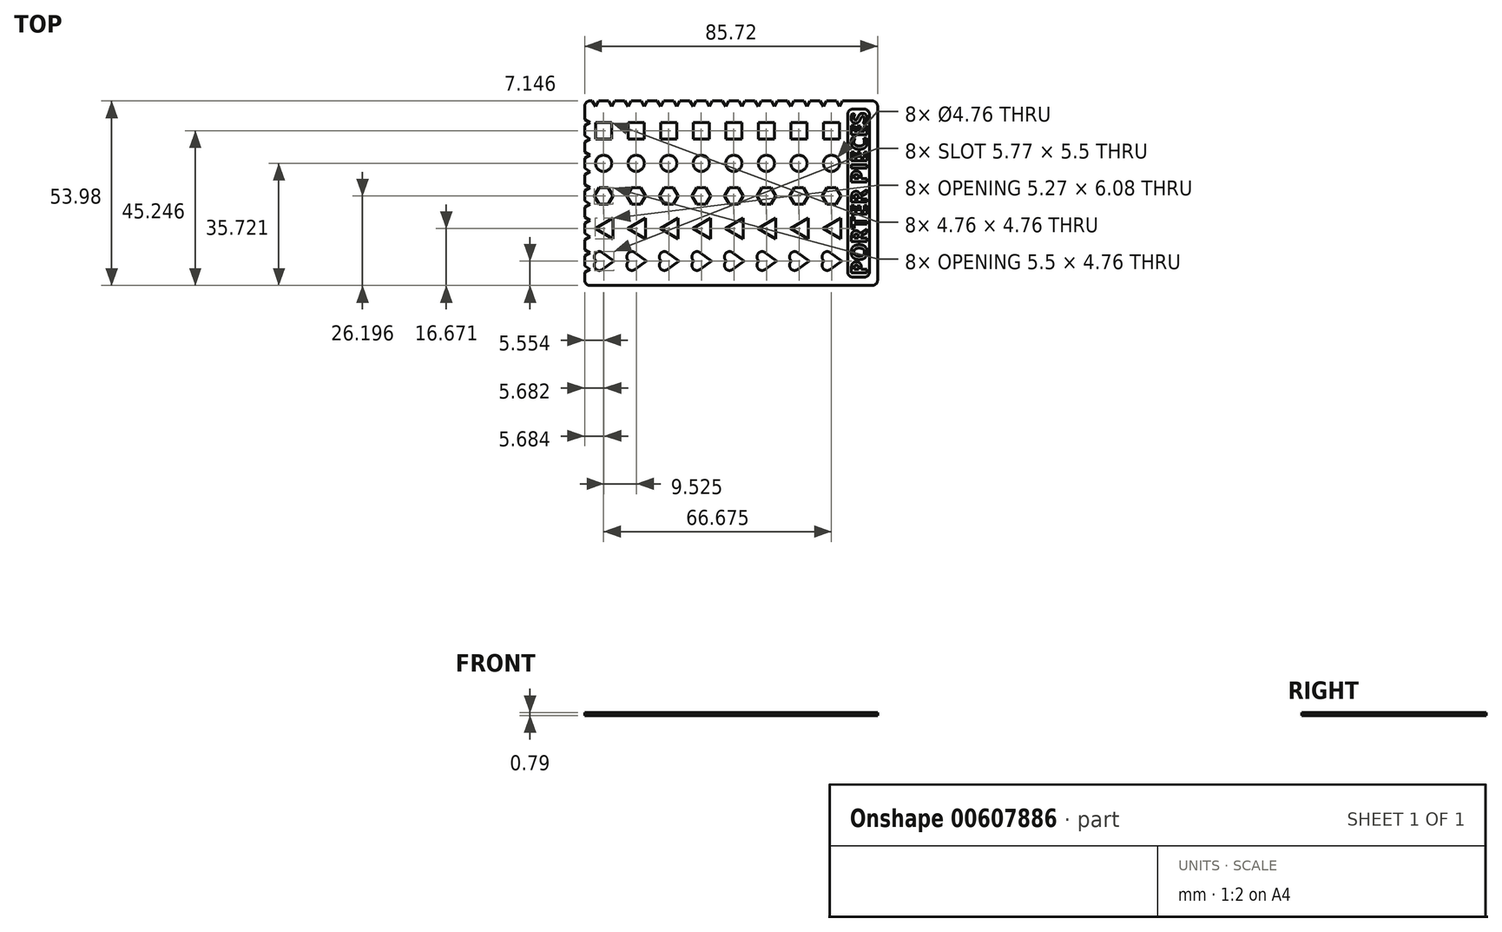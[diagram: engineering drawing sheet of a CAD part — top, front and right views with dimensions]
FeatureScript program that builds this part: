
annotation { "Feature Type Name" : "Feature", "Feature Type Description" : "" }
export const myFeature = defineFeature(function(context is Context, id is Id, definition is map)
    precondition{}
    {
        {
            var Q0;
            Q0=qCreatedBy(makeId("Top.planeOp"),FACE);
            var sketch = newSketch(context, id + "F0", { "sketchPlane" : qUnion([Q0])});
            skLineSegment(sketch, "E0.bottom", {"start": v(42.86, 26.99) * mm, "end": v(-42.86, 26.99) * mm});
            skLineSegment(sketch, "E0.top", {"start": v(42.86, -26.99) * mm, "end": v(-42.86, -26.99) * mm});
            skLineSegment(sketch, "E0.left", {"start": v(42.86, 26.99) * mm, "end": v(42.86, -26.99) * mm});
            skLineSegment(sketch, "E0.right", {"start": v(-42.86, 26.99) * mm, "end": v(-42.86, -26.99) * mm});
            skPoint(sketch, "E0.middle", {"position": v(0, 0) * mm});
            skSolve(sketch);
        }
        {
            var Q0;
            Q0=makeQuery(id+"F0.imprint","IMPRINT",FACE,{"disambiguationData":[TD([[makeQuery(id+"F0.imprint","IMPRINT",EDGE,{"derivedFrom":sQuery(id+"F0.wireOp",EDGE,"E0.bottom")}),1.0]])]});
            extrude(context, id + "F1", {"entities" : qUnion([Q0]), "depth" : 0.8 * mm, "offsetDistance" : 25.4 * mm});
        }
        {
            var Q0;
            Q0=makeQuery(id+"F1.opExtrude","SWEPT_EDGE",EDGE,{"disambiguationData":[OSD([sQuery(id+"F0.wireOp",EDGE,"E0.bottom"),sQuery(id+"F0.wireOp",EDGE,"E0.left")])]});
            var Q1;
            Q1=makeQuery(id+"F1.opExtrude","SWEPT_EDGE",EDGE,{"disambiguationData":[OSD([sQuery(id+"F0.wireOp",EDGE,"E0.bottom"),sQuery(id+"F0.wireOp",EDGE,"E0.right")])]});
            var Q2;
            Q2=makeQuery(id+"F1.opExtrude","SWEPT_EDGE",EDGE,{"disambiguationData":[OSD([sQuery(id+"F0.wireOp",EDGE,"E0.top"),sQuery(id+"F0.wireOp",EDGE,"E0.right")])]});
            var Q3;
            Q3=makeQuery(id+"F1.opExtrude","SWEPT_EDGE",EDGE,{"disambiguationData":[OSD([sQuery(id+"F0.wireOp",EDGE,"E0.top"),sQuery(id+"F0.wireOp",EDGE,"E0.left")])]});
            fillet(context, id + "F2", {"entities" : qUnion([Q0, Q1, Q2, Q3]), "radius" : 1.59 * mm, "tangentPropagation" : true, "allowEdgeOverflow" : false});
        }
        {
            var Q0;
            Q0=makeQuery(id+"F1.opExtrude","CAP_FACE",FACE,{"disambiguationData":[OSD([sQuery(id+"F0.wireOp",EDGE,"E0.bottom"),sQuery(id+"F0.wireOp",EDGE,"E0.top"),sQuery(id+"F0.wireOp",EDGE,"E0.left"),sQuery(id+"F0.wireOp",EDGE,"E0.right")])],"isStart":false});
            var sketch = newSketch(context, id + "F3", { "sketchPlane" : qUnion([Q0])});
            skLineSegment(sketch, "E1.bottom", {"start": v(-39.69, 20.64) * mm, "end": v(-34.92, 20.64) * mm});
            skLineSegment(sketch, "E1.top", {"start": v(-39.69, 15.88) * mm, "end": v(-34.92, 15.88) * mm});
            skLineSegment(sketch, "E1.left", {"start": v(-39.69, 20.64) * mm, "end": v(-39.69, 15.88) * mm});
            skLineSegment(sketch, "E1.right", {"start": v(-34.92, 20.64) * mm, "end": v(-34.92, 15.88) * mm});
            skLineSegment(sketch, "E2.1.0.0", {"start": v(-25.4, 20.64) * mm, "end": v(-25.4, 15.88) * mm});
            skLineSegment(sketch, "E2.1.0.1", {"start": v(-30.16, 20.64) * mm, "end": v(-30.16, 15.88) * mm});
            skLineSegment(sketch, "E2.1.0.2", {"start": v(-30.16, 15.88) * mm, "end": v(-25.4, 15.88) * mm});
            skLineSegment(sketch, "E2.1.0.3", {"start": v(-30.16, 20.64) * mm, "end": v(-25.4, 20.64) * mm});
            skLineSegment(sketch, "E2.2.0.0", {"start": v(-15.88, 20.64) * mm, "end": v(-15.88, 15.88) * mm});
            skLineSegment(sketch, "E2.2.0.1", {"start": v(-20.64, 20.64) * mm, "end": v(-20.64, 15.88) * mm});
            skLineSegment(sketch, "E2.2.0.2", {"start": v(-20.64, 15.88) * mm, "end": v(-15.88, 15.88) * mm});
            skLineSegment(sketch, "E2.2.0.3", {"start": v(-20.64, 20.64) * mm, "end": v(-15.88, 20.64) * mm});
            skLineSegment(sketch, "E2.3.0.0", {"start": v(-6.35, 20.64) * mm, "end": v(-6.35, 15.88) * mm});
            skLineSegment(sketch, "E2.3.0.1", {"start": v(-11.11, 20.64) * mm, "end": v(-11.11, 15.88) * mm});
            skLineSegment(sketch, "E2.3.0.2", {"start": v(-11.11, 15.88) * mm, "end": v(-6.35, 15.88) * mm});
            skLineSegment(sketch, "E2.3.0.3", {"start": v(-11.11, 20.64) * mm, "end": v(-6.35, 20.64) * mm});
            skLineSegment(sketch, "E2.4.0.0", {"start": v(3.17, 20.64) * mm, "end": v(3.17, 15.88) * mm});
            skLineSegment(sketch, "E2.4.0.1", {"start": v(-1.59, 20.64) * mm, "end": v(-1.59, 15.88) * mm});
            skLineSegment(sketch, "E2.4.0.2", {"start": v(-1.59, 15.88) * mm, "end": v(3.17, 15.88) * mm});
            skLineSegment(sketch, "E2.4.0.3", {"start": v(-1.59, 20.64) * mm, "end": v(3.17, 20.64) * mm});
            skLineSegment(sketch, "E2.5.0.0", {"start": v(12.7, 20.64) * mm, "end": v(12.7, 15.88) * mm});
            skLineSegment(sketch, "E2.5.0.1", {"start": v(7.94, 20.64) * mm, "end": v(7.94, 15.88) * mm});
            skLineSegment(sketch, "E2.5.0.2", {"start": v(7.94, 15.88) * mm, "end": v(12.7, 15.88) * mm});
            skLineSegment(sketch, "E2.5.0.3", {"start": v(7.94, 20.64) * mm, "end": v(12.7, 20.64) * mm});
            skLineSegment(sketch, "E2.6.0.0", {"start": v(22.22, 20.64) * mm, "end": v(22.22, 15.88) * mm});
            skLineSegment(sketch, "E2.6.0.1", {"start": v(17.46, 20.64) * mm, "end": v(17.46, 15.88) * mm});
            skLineSegment(sketch, "E2.6.0.2", {"start": v(17.46, 15.88) * mm, "end": v(22.22, 15.88) * mm});
            skLineSegment(sketch, "E2.6.0.3", {"start": v(17.46, 20.64) * mm, "end": v(22.22, 20.64) * mm});
            skLineSegment(sketch, "E2.7.0.0", {"start": v(31.75, 20.64) * mm, "end": v(31.75, 15.88) * mm});
            skLineSegment(sketch, "E2.7.0.1", {"start": v(26.99, 20.64) * mm, "end": v(26.99, 15.88) * mm});
            skLineSegment(sketch, "E2.7.0.2", {"start": v(26.99, 15.88) * mm, "end": v(31.75, 15.88) * mm});
            skLineSegment(sketch, "E2.7.0.3", {"start": v(26.99, 20.64) * mm, "end": v(31.75, 20.64) * mm});
            skLineSegment(sketch, "E2.direction1", {"start": v(-39.69, 15.88) * mm, "end": v(-30.16, 15.88) * mm, "construction": true});
            skSolve(sketch);
        }
        {
            var Q0;
            Q0=makeQuery(id+"F3.imprint","IMPRINT",FACE,{"disambiguationData":[TD([[makeQuery(id+"F3.imprint","IMPRINT",EDGE,{"derivedFrom":sQuery(id+"F3.wireOp",EDGE,"E1.bottom")}),-1.0]])]});
            var Q1;
            Q1=makeQuery(id+"F3.imprint","IMPRINT",FACE,{"disambiguationData":[TD([[makeQuery(id+"F3.imprint","IMPRINT",EDGE,{"derivedFrom":sQuery(id+"F3.wireOp",EDGE,"E2.1.0.0")}),-1.0]])]});
            var Q2;
            Q2=makeQuery(id+"F3.imprint","IMPRINT",FACE,{"disambiguationData":[TD([[makeQuery(id+"F3.imprint","IMPRINT",EDGE,{"derivedFrom":sQuery(id+"F3.wireOp",EDGE,"E2.2.0.0")}),-1.0]])]});
            var Q3;
            Q3=makeQuery(id+"F3.imprint","IMPRINT",FACE,{"disambiguationData":[TD([[makeQuery(id+"F3.imprint","IMPRINT",EDGE,{"derivedFrom":sQuery(id+"F3.wireOp",EDGE,"E2.3.0.0")}),-1.0]])]});
            var Q4;
            Q4=makeQuery(id+"F3.imprint","IMPRINT",FACE,{"disambiguationData":[TD([[makeQuery(id+"F3.imprint","IMPRINT",EDGE,{"derivedFrom":sQuery(id+"F3.wireOp",EDGE,"E2.4.0.0")}),-1.0]])]});
            var Q5;
            Q5=makeQuery(id+"F3.imprint","IMPRINT",FACE,{"disambiguationData":[TD([[makeQuery(id+"F3.imprint","IMPRINT",EDGE,{"derivedFrom":sQuery(id+"F3.wireOp",EDGE,"E2.5.0.0")}),-1.0]])]});
            var Q6;
            Q6=makeQuery(id+"F3.imprint","IMPRINT",FACE,{"disambiguationData":[TD([[makeQuery(id+"F3.imprint","IMPRINT",EDGE,{"derivedFrom":sQuery(id+"F3.wireOp",EDGE,"E2.6.0.0")}),-1.0]])]});
            var Q7;
            Q7=makeQuery(id+"F3.imprint","IMPRINT",FACE,{"disambiguationData":[TD([[makeQuery(id+"F3.imprint","IMPRINT",EDGE,{"derivedFrom":sQuery(id+"F3.wireOp",EDGE,"E2.7.0.0")}),-1.0]])]});
            var Q8;
            Q8=makeQuery(id+"F3.imprint","IMPRINT",FACE,{"disambiguationData":[TD([[makeQuery(id+"F3.imprint","IMPRINT",EDGE,{"derivedFrom":sQuery(id+"F3.wireOp",EDGE,"E2.8.0.0")}),-1.0]])]});
            extrude(context, id + "F4", {"entities" : qUnion([Q0, Q1, Q2, Q3, Q4, Q5, Q6, Q7, Q8]), "operationType" : NewBodyOperationType.REMOVE, "oppositeDirection" : true, "depth" : 25.4 * mm, "offsetDistance" : 25.4 * mm});
        }
        {
            var Q0;
            Q0=makeQuery(id+"F1.opExtrude","CAP_FACE",FACE,{"disambiguationData":[OSD([sQuery(id+"F0.wireOp",EDGE,"E0.bottom"),sQuery(id+"F0.wireOp",EDGE,"E0.top"),sQuery(id+"F0.wireOp",EDGE,"E0.left"),sQuery(id+"F0.wireOp",EDGE,"E0.right")])],"isStart":false});
            var sketch = newSketch(context, id + "F5", { "sketchPlane" : qUnion([Q0])});
            skLineSegment(sketch, "E3", {"start": v(-34.92, 25.44) * mm, "end": v(-34.92, 26.99) * mm, "construction": true});
            skLineSegment(sketch, "E4.0", {"start": v(41.27, 26.99) * mm, "end": v(-41.28, 26.99) * mm, "construction": true});
            skLineSegment(sketch, "E5", {"start": v(-34.92, 26.99) * mm, "end": v(-34.92, 34.22) * mm, "construction": true});
            skCircle(sketch, "E6.cCircle", {"center": v(-34.92, 26.99) * mm, "radius": 0.8 * mm, "construction": true});
            skLineSegment(sketch, "E6.0", {"start": v(-36.3, 27.78) * mm, "end": v(-33.55, 27.78) * mm});
            skLineSegment(sketch, "E6.1", {"start": v(-33.55, 27.78) * mm, "end": v(-34.93, 25.4) * mm});
            skLineSegment(sketch, "E6.2", {"start": v(-34.92, 25.4) * mm, "end": v(-36.3, 27.78) * mm});
            skPoint(sketch, "E6.0.midPoint", {"position": v(-34.92, 27.78) * mm});
            skPoint(sketch, "E7.1.0.0", {"position": v(-30.16, 27.78) * mm});
            skLineSegment(sketch, "E7.1.0.1", {"start": v(-30.16, 25.4) * mm, "end": v(-31.54, 27.78) * mm});
            skLineSegment(sketch, "E7.1.0.2", {"start": v(-28.79, 27.78) * mm, "end": v(-30.16, 25.4) * mm});
            skLineSegment(sketch, "E7.1.0.3", {"start": v(-31.54, 27.78) * mm, "end": v(-28.79, 27.78) * mm});
            skCircle(sketch, "E7.1.0.4", {"center": v(-30.16, 26.99) * mm, "radius": 0.8 * mm, "construction": true});
            skPoint(sketch, "E7.2.0.0", {"position": v(-25.4, 27.78) * mm});
            skLineSegment(sketch, "E7.2.0.1", {"start": v(-25.4, 25.4) * mm, "end": v(-26.77, 27.78) * mm});
            skLineSegment(sketch, "E7.2.0.2", {"start": v(-24.03, 27.78) * mm, "end": v(-25.4, 25.4) * mm});
            skLineSegment(sketch, "E7.2.0.3", {"start": v(-26.77, 27.78) * mm, "end": v(-24.03, 27.78) * mm});
            skCircle(sketch, "E7.2.0.4", {"center": v(-25.4, 26.99) * mm, "radius": 0.8 * mm, "construction": true});
            skPoint(sketch, "E7.3.0.0", {"position": v(-20.64, 27.78) * mm});
            skLineSegment(sketch, "E7.3.0.1", {"start": v(-20.64, 25.4) * mm, "end": v(-22.01, 27.78) * mm});
            skLineSegment(sketch, "E7.3.0.2", {"start": v(-19.26, 27.78) * mm, "end": v(-20.64, 25.4) * mm});
            skLineSegment(sketch, "E7.3.0.3", {"start": v(-22.01, 27.78) * mm, "end": v(-19.26, 27.78) * mm});
            skCircle(sketch, "E7.3.0.4", {"center": v(-20.64, 26.99) * mm, "radius": 0.8 * mm, "construction": true});
            skPoint(sketch, "E7.4.0.0", {"position": v(-15.87, 27.78) * mm});
            skLineSegment(sketch, "E7.4.0.1", {"start": v(-15.87, 25.4) * mm, "end": v(-17.25, 27.78) * mm});
            skLineSegment(sketch, "E7.4.0.2", {"start": v(-14.5, 27.78) * mm, "end": v(-15.87, 25.4) * mm});
            skLineSegment(sketch, "E7.4.0.3", {"start": v(-17.25, 27.78) * mm, "end": v(-14.5, 27.78) * mm});
            skCircle(sketch, "E7.4.0.4", {"center": v(-15.87, 26.99) * mm, "radius": 0.8 * mm, "construction": true});
            skPoint(sketch, "E7.5.0.0", {"position": v(-11.11, 27.78) * mm});
            skLineSegment(sketch, "E7.5.0.1", {"start": v(-11.11, 25.4) * mm, "end": v(-12.49, 27.78) * mm});
            skLineSegment(sketch, "E7.5.0.2", {"start": v(-9.74, 27.78) * mm, "end": v(-11.11, 25.4) * mm});
            skLineSegment(sketch, "E7.5.0.3", {"start": v(-12.49, 27.78) * mm, "end": v(-9.74, 27.78) * mm});
            skCircle(sketch, "E7.5.0.4", {"center": v(-11.11, 26.99) * mm, "radius": 0.8 * mm, "construction": true});
            skPoint(sketch, "E7.6.0.0", {"position": v(-6.35, 27.78) * mm});
            skLineSegment(sketch, "E7.6.0.1", {"start": v(-6.35, 25.4) * mm, "end": v(-7.72, 27.78) * mm});
            skLineSegment(sketch, "E7.6.0.2", {"start": v(-4.98, 27.78) * mm, "end": v(-6.35, 25.4) * mm});
            skLineSegment(sketch, "E7.6.0.3", {"start": v(-7.72, 27.78) * mm, "end": v(-4.98, 27.78) * mm});
            skCircle(sketch, "E7.6.0.4", {"center": v(-6.35, 26.99) * mm, "radius": 0.8 * mm, "construction": true});
            skPoint(sketch, "E7.7.0.0", {"position": v(-1.59, 27.78) * mm});
            skLineSegment(sketch, "E7.7.0.1", {"start": v(-1.59, 25.4) * mm, "end": v(-2.96, 27.78) * mm});
            skLineSegment(sketch, "E7.7.0.2", {"start": v(-0.21, 27.78) * mm, "end": v(-1.59, 25.4) * mm});
            skLineSegment(sketch, "E7.7.0.3", {"start": v(-2.96, 27.78) * mm, "end": v(-0.21, 27.78) * mm});
            skCircle(sketch, "E7.7.0.4", {"center": v(-1.59, 26.99) * mm, "radius": 0.8 * mm, "construction": true});
            skPoint(sketch, "E7.8.0.0", {"position": v(3.18, 27.78) * mm});
            skLineSegment(sketch, "E7.8.0.1", {"start": v(3.18, 25.4) * mm, "end": v(1.8, 27.78) * mm});
            skLineSegment(sketch, "E7.8.0.2", {"start": v(4.55, 27.78) * mm, "end": v(3.18, 25.4) * mm});
            skLineSegment(sketch, "E7.8.0.3", {"start": v(1.8, 27.78) * mm, "end": v(4.55, 27.78) * mm});
            skCircle(sketch, "E7.8.0.4", {"center": v(3.18, 26.99) * mm, "radius": 0.8 * mm, "construction": true});
            skPoint(sketch, "E7.9.0.0", {"position": v(7.94, 27.78) * mm});
            skLineSegment(sketch, "E7.9.0.1", {"start": v(7.94, 25.4) * mm, "end": v(6.56, 27.78) * mm});
            skLineSegment(sketch, "E7.9.0.2", {"start": v(9.31, 27.78) * mm, "end": v(7.94, 25.4) * mm});
            skLineSegment(sketch, "E7.9.0.3", {"start": v(6.56, 27.78) * mm, "end": v(9.31, 27.78) * mm});
            skCircle(sketch, "E7.9.0.4", {"center": v(7.94, 26.99) * mm, "radius": 0.8 * mm, "construction": true});
            skPoint(sketch, "E7.10.0.0", {"position": v(12.7, 27.78) * mm});
            skLineSegment(sketch, "E7.10.0.1", {"start": v(12.7, 25.4) * mm, "end": v(11.33, 27.78) * mm});
            skLineSegment(sketch, "E7.10.0.2", {"start": v(14.07, 27.78) * mm, "end": v(12.7, 25.4) * mm});
            skLineSegment(sketch, "E7.10.0.3", {"start": v(11.33, 27.78) * mm, "end": v(14.07, 27.78) * mm});
            skCircle(sketch, "E7.10.0.4", {"center": v(12.7, 26.99) * mm, "radius": 0.8 * mm, "construction": true});
            skPoint(sketch, "E7.11.0.0", {"position": v(17.46, 27.78) * mm});
            skLineSegment(sketch, "E7.11.0.1", {"start": v(17.46, 25.4) * mm, "end": v(16.09, 27.78) * mm});
            skLineSegment(sketch, "E7.11.0.2", {"start": v(18.84, 27.78) * mm, "end": v(17.46, 25.4) * mm});
            skLineSegment(sketch, "E7.11.0.3", {"start": v(16.09, 27.78) * mm, "end": v(18.84, 27.78) * mm});
            skCircle(sketch, "E7.11.0.4", {"center": v(17.46, 26.99) * mm, "radius": 0.8 * mm, "construction": true});
            skPoint(sketch, "E7.12.0.0", {"position": v(22.23, 27.78) * mm});
            skLineSegment(sketch, "E7.12.0.1", {"start": v(22.23, 25.4) * mm, "end": v(20.85, 27.78) * mm});
            skLineSegment(sketch, "E7.12.0.2", {"start": v(23.6, 27.78) * mm, "end": v(22.23, 25.4) * mm});
            skLineSegment(sketch, "E7.12.0.3", {"start": v(20.85, 27.78) * mm, "end": v(23.6, 27.78) * mm});
            skCircle(sketch, "E7.12.0.4", {"center": v(22.23, 26.99) * mm, "radius": 0.8 * mm, "construction": true});
            skPoint(sketch, "E7.13.0.0", {"position": v(26.99, 27.78) * mm});
            skLineSegment(sketch, "E7.13.0.1", {"start": v(26.99, 25.4) * mm, "end": v(25.61, 27.78) * mm});
            skLineSegment(sketch, "E7.13.0.2", {"start": v(28.36, 27.78) * mm, "end": v(26.99, 25.4) * mm});
            skLineSegment(sketch, "E7.13.0.3", {"start": v(25.61, 27.78) * mm, "end": v(28.36, 27.78) * mm});
            skCircle(sketch, "E7.13.0.4", {"center": v(26.99, 26.99) * mm, "radius": 0.8 * mm, "construction": true});
            skPoint(sketch, "E7.14.0.0", {"position": v(31.75, 27.78) * mm});
            skLineSegment(sketch, "E7.14.0.1", {"start": v(31.75, 25.4) * mm, "end": v(30.38, 27.78) * mm});
            skLineSegment(sketch, "E7.14.0.2", {"start": v(33.12, 27.78) * mm, "end": v(31.75, 25.4) * mm});
            skLineSegment(sketch, "E7.14.0.3", {"start": v(30.38, 27.78) * mm, "end": v(33.12, 27.78) * mm});
            skCircle(sketch, "E7.14.0.4", {"center": v(31.75, 26.99) * mm, "radius": 0.8 * mm, "construction": true});
            skLineSegment(sketch, "E7.direction1", {"start": v(-34.92, 25.4) * mm, "end": v(-30.16, 25.4) * mm, "construction": true});
            skSolve(sketch);
        }
        {
            var Q0;
            {var subQ0=sQuery(id+"F5.wireOp",EDGE,"E6.2");var subQ1=sQuery(id+"F5.wireOp",EDGE,"E6.1");var subQ2=makeQuery(id+"F5.imprint","INTERSECT",VERTEX,{"derivedFrom":[subQ1,subQ0]});Q0=makeQuery(id+"F5.imprint","IMPRINT",FACE,{"disambiguationData":[TD([[makeQuery(id+"F5.imprint","IMPRINT",EDGE,{"disambiguationData":[TD([[subQ2,1.0]])],"derivedFrom":subQ1}),-1.0]])]});}
            var Q1;
            {var subQ0=sQuery(id+"F5.wireOp",EDGE,"E7.1.0.2");var subQ1=sQuery(id+"F5.wireOp",EDGE,"E7.1.0.1");var subQ2=makeQuery(id+"F5.imprint","INTERSECT",VERTEX,{"derivedFrom":[subQ1,subQ0]});Q1=makeQuery(id+"F5.imprint","IMPRINT",FACE,{"disambiguationData":[TD([[makeQuery(id+"F5.imprint","IMPRINT",EDGE,{"disambiguationData":[TD([[subQ2,-1.0]])],"derivedFrom":subQ1}),-1.0]])]});}
            var Q2;
            {var subQ0=sQuery(id+"F5.wireOp",EDGE,"E7.2.0.2");var subQ1=sQuery(id+"F5.wireOp",EDGE,"E7.2.0.1");var subQ2=makeQuery(id+"F5.imprint","INTERSECT",VERTEX,{"derivedFrom":[subQ1,subQ0]});Q2=makeQuery(id+"F5.imprint","IMPRINT",FACE,{"disambiguationData":[TD([[makeQuery(id+"F5.imprint","IMPRINT",EDGE,{"disambiguationData":[TD([[subQ2,-1.0]])],"derivedFrom":subQ1}),-1.0]])]});}
            var Q3;
            {var subQ0=sQuery(id+"F5.wireOp",EDGE,"E7.3.0.2");var subQ1=sQuery(id+"F5.wireOp",EDGE,"E7.3.0.1");var subQ2=makeQuery(id+"F5.imprint","INTERSECT",VERTEX,{"derivedFrom":[subQ1,subQ0]});Q3=makeQuery(id+"F5.imprint","IMPRINT",FACE,{"disambiguationData":[TD([[makeQuery(id+"F5.imprint","IMPRINT",EDGE,{"disambiguationData":[TD([[subQ2,-1.0]])],"derivedFrom":subQ1}),-1.0]])]});}
            var Q4;
            {var subQ0=sQuery(id+"F5.wireOp",EDGE,"E7.4.0.2");var subQ1=sQuery(id+"F5.wireOp",EDGE,"E7.4.0.1");var subQ2=makeQuery(id+"F5.imprint","INTERSECT",VERTEX,{"derivedFrom":[subQ1,subQ0]});Q4=makeQuery(id+"F5.imprint","IMPRINT",FACE,{"disambiguationData":[TD([[makeQuery(id+"F5.imprint","IMPRINT",EDGE,{"disambiguationData":[TD([[subQ2,-1.0]])],"derivedFrom":subQ1}),-1.0]])]});}
            var Q5;
            {var subQ0=sQuery(id+"F5.wireOp",EDGE,"E7.5.0.2");var subQ1=sQuery(id+"F5.wireOp",EDGE,"E7.5.0.1");var subQ2=makeQuery(id+"F5.imprint","INTERSECT",VERTEX,{"derivedFrom":[subQ1,subQ0]});Q5=makeQuery(id+"F5.imprint","IMPRINT",FACE,{"disambiguationData":[TD([[makeQuery(id+"F5.imprint","IMPRINT",EDGE,{"disambiguationData":[TD([[subQ2,-1.0]])],"derivedFrom":subQ1}),-1.0]])]});}
            var Q6;
            {var subQ0=sQuery(id+"F5.wireOp",EDGE,"E7.6.0.2");var subQ1=sQuery(id+"F5.wireOp",EDGE,"E7.6.0.1");var subQ2=makeQuery(id+"F5.imprint","INTERSECT",VERTEX,{"derivedFrom":[subQ1,subQ0]});Q6=makeQuery(id+"F5.imprint","IMPRINT",FACE,{"disambiguationData":[TD([[makeQuery(id+"F5.imprint","IMPRINT",EDGE,{"disambiguationData":[TD([[subQ2,-1.0]])],"derivedFrom":subQ1}),-1.0]])]});}
            var Q7;
            {var subQ0=sQuery(id+"F5.wireOp",EDGE,"E7.7.0.2");var subQ1=sQuery(id+"F5.wireOp",EDGE,"E7.7.0.1");var subQ2=makeQuery(id+"F5.imprint","INTERSECT",VERTEX,{"derivedFrom":[subQ1,subQ0]});Q7=makeQuery(id+"F5.imprint","IMPRINT",FACE,{"disambiguationData":[TD([[makeQuery(id+"F5.imprint","IMPRINT",EDGE,{"disambiguationData":[TD([[subQ2,-1.0]])],"derivedFrom":subQ1}),-1.0]])]});}
            var Q8;
            {var subQ0=sQuery(id+"F5.wireOp",EDGE,"E7.9.0.2");var subQ1=sQuery(id+"F5.wireOp",EDGE,"E7.9.0.1");var subQ2=makeQuery(id+"F5.imprint","INTERSECT",VERTEX,{"derivedFrom":[subQ1,subQ0]});Q8=makeQuery(id+"F5.imprint","IMPRINT",FACE,{"disambiguationData":[TD([[makeQuery(id+"F5.imprint","IMPRINT",EDGE,{"disambiguationData":[TD([[subQ2,-1.0]])],"derivedFrom":subQ1}),-1.0]])]});}
            var Q9;
            {var subQ0=sQuery(id+"F5.wireOp",EDGE,"E7.8.0.2");var subQ1=sQuery(id+"F5.wireOp",EDGE,"E7.8.0.1");var subQ2=makeQuery(id+"F5.imprint","INTERSECT",VERTEX,{"derivedFrom":[subQ1,subQ0]});Q9=makeQuery(id+"F5.imprint","IMPRINT",FACE,{"disambiguationData":[TD([[makeQuery(id+"F5.imprint","IMPRINT",EDGE,{"disambiguationData":[TD([[subQ2,-1.0]])],"derivedFrom":subQ1}),-1.0]])]});}
            var Q10;
            {var subQ0=sQuery(id+"F5.wireOp",EDGE,"E7.10.0.2");var subQ1=sQuery(id+"F5.wireOp",EDGE,"E7.10.0.1");var subQ2=makeQuery(id+"F5.imprint","INTERSECT",VERTEX,{"derivedFrom":[subQ1,subQ0]});Q10=makeQuery(id+"F5.imprint","IMPRINT",FACE,{"disambiguationData":[TD([[makeQuery(id+"F5.imprint","IMPRINT",EDGE,{"disambiguationData":[TD([[subQ2,-1.0]])],"derivedFrom":subQ1}),-1.0]])]});}
            var Q11;
            {var subQ0=sQuery(id+"F5.wireOp",EDGE,"E7.11.0.2");var subQ1=sQuery(id+"F5.wireOp",EDGE,"E7.11.0.1");var subQ2=makeQuery(id+"F5.imprint","INTERSECT",VERTEX,{"derivedFrom":[subQ1,subQ0]});Q11=makeQuery(id+"F5.imprint","IMPRINT",FACE,{"disambiguationData":[TD([[makeQuery(id+"F5.imprint","IMPRINT",EDGE,{"disambiguationData":[TD([[subQ2,-1.0]])],"derivedFrom":subQ1}),-1.0]])]});}
            var Q12;
            {var subQ0=sQuery(id+"F5.wireOp",EDGE,"E7.16.0.2");var subQ1=sQuery(id+"F5.wireOp",EDGE,"E7.16.0.1");var subQ2=makeQuery(id+"F5.imprint","INTERSECT",VERTEX,{"derivedFrom":[subQ1,subQ0]});Q12=makeQuery(id+"F5.imprint","IMPRINT",FACE,{"disambiguationData":[TD([[makeQuery(id+"F5.imprint","IMPRINT",EDGE,{"disambiguationData":[TD([[subQ2,-1.0]])],"derivedFrom":subQ1}),-1.0]])]});}
            var Q13;
            {var subQ0=sQuery(id+"F5.wireOp",EDGE,"E7.15.0.2");var subQ1=sQuery(id+"F5.wireOp",EDGE,"E7.15.0.1");var subQ2=makeQuery(id+"F5.imprint","INTERSECT",VERTEX,{"derivedFrom":[subQ1,subQ0]});Q13=makeQuery(id+"F5.imprint","IMPRINT",FACE,{"disambiguationData":[TD([[makeQuery(id+"F5.imprint","IMPRINT",EDGE,{"disambiguationData":[TD([[subQ2,-1.0]])],"derivedFrom":subQ1}),-1.0]])]});}
            var Q14;
            {var subQ0=sQuery(id+"F5.wireOp",EDGE,"E7.14.0.2");var subQ1=sQuery(id+"F5.wireOp",EDGE,"E7.14.0.1");var subQ2=makeQuery(id+"F5.imprint","INTERSECT",VERTEX,{"derivedFrom":[subQ1,subQ0]});Q14=makeQuery(id+"F5.imprint","IMPRINT",FACE,{"disambiguationData":[TD([[makeQuery(id+"F5.imprint","IMPRINT",EDGE,{"disambiguationData":[TD([[subQ2,-1.0]])],"derivedFrom":subQ1}),-1.0]])]});}
            var Q15;
            {var subQ0=sQuery(id+"F5.wireOp",EDGE,"E7.13.0.2");var subQ1=sQuery(id+"F5.wireOp",EDGE,"E7.13.0.1");var subQ2=makeQuery(id+"F5.imprint","INTERSECT",VERTEX,{"derivedFrom":[subQ1,subQ0]});Q15=makeQuery(id+"F5.imprint","IMPRINT",FACE,{"disambiguationData":[TD([[makeQuery(id+"F5.imprint","IMPRINT",EDGE,{"disambiguationData":[TD([[subQ2,-1.0]])],"derivedFrom":subQ1}),-1.0]])]});}
            var Q16;
            {var subQ0=sQuery(id+"F5.wireOp",EDGE,"E7.12.0.2");var subQ1=sQuery(id+"F5.wireOp",EDGE,"E7.12.0.1");var subQ2=makeQuery(id+"F5.imprint","INTERSECT",VERTEX,{"derivedFrom":[subQ1,subQ0]});Q16=makeQuery(id+"F5.imprint","IMPRINT",FACE,{"disambiguationData":[TD([[makeQuery(id+"F5.imprint","IMPRINT",EDGE,{"disambiguationData":[TD([[subQ2,-1.0]])],"derivedFrom":subQ1}),-1.0]])]});}
            extrude(context, id + "F6", {"entities" : qUnion([Q0, Q1, Q2, Q3, Q4, Q5, Q6, Q7, Q8, Q9, Q10, Q11, Q12, Q13, Q14, Q15, Q16]), "operationType" : NewBodyOperationType.REMOVE, "oppositeDirection" : true, "depth" : 25.4 * mm, "offsetDistance" : 25.4 * mm});
        }
        {
            var Q0;
            Q0=makeQuery(id+"F1.opExtrude","CAP_FACE",FACE,{"disambiguationData":[OSD([sQuery(id+"F0.wireOp",EDGE,"E0.bottom"),sQuery(id+"F0.wireOp",EDGE,"E0.top"),sQuery(id+"F0.wireOp",EDGE,"E0.left"),sQuery(id+"F0.wireOp",EDGE,"E0.right")])],"isStart":false});
            var sketch = newSketch(context, id + "F7", { "sketchPlane" : qUnion([Q0])});
            skLineSegment(sketch, "E8", {"start": v(-39.69, 20.64) * mm, "end": v(-39.69, 30.6) * mm, "construction": true});
            skLineSegment(sketch, "E9.0", {"start": v(-35.84, 26.99) * mm, "end": v(-41.28, 26.99) * mm, "construction": true});
            skCircle(sketch, "E10.cCircle", {"center": v(-39.69, 26.99) * mm, "radius": 0.8 * mm, "construction": true});
            skLineSegment(sketch, "E10.0", {"start": v(-41.06, 27.78) * mm, "end": v(-38.31, 27.78) * mm});
            skLineSegment(sketch, "E10.1", {"start": v(-38.31, 27.78) * mm, "end": v(-39.69, 25.4) * mm});
            skLineSegment(sketch, "E10.2", {"start": v(-39.69, 25.4) * mm, "end": v(-41.06, 27.78) * mm});
            skPoint(sketch, "E10.0.midPoint", {"position": v(-39.69, 27.78) * mm});
            skSolve(sketch);
        }
        {
            var Q0;
            {var subQ0=sQuery(id+"F7.wireOp",EDGE,"E10.2");var subQ1=sQuery(id+"F7.wireOp",EDGE,"E10.1");var subQ2=makeQuery(id+"F7.imprint","INTERSECT",VERTEX,{"derivedFrom":[subQ1,subQ0]});Q0=makeQuery(id+"F7.imprint","IMPRINT",FACE,{"disambiguationData":[TD([[makeQuery(id+"F7.imprint","IMPRINT",EDGE,{"disambiguationData":[TD([[subQ2,1.0]])],"derivedFrom":subQ1}),-1.0]])]});}
            extrude(context, id + "F8", {"entities" : qUnion([Q0]), "operationType" : NewBodyOperationType.REMOVE, "oppositeDirection" : true, "depth" : 25.4 * mm, "offsetDistance" : 25.4 * mm});
        }
        {
            var Q0;
            Q0=makeQuery(id+"F1.opExtrude","CAP_FACE",FACE,{"disambiguationData":[OSD([sQuery(id+"F0.wireOp",EDGE,"E0.bottom"),sQuery(id+"F0.wireOp",EDGE,"E0.top"),sQuery(id+"F0.wireOp",EDGE,"E0.left"),sQuery(id+"F0.wireOp",EDGE,"E0.right")])],"isStart":false});
            var sketch = newSketch(context, id + "F9", { "sketchPlane" : qUnion([Q0])});
            skLineSegment(sketch, "E11", {"start": v(-37.3, 20.64) * mm, "end": v(-37.3, 8.98) * mm, "construction": true});
            skLineSegment(sketch, "E12", {"start": v(-42.86, 8.73) * mm, "end": v(-29.74, 8.73) * mm, "construction": true});
            skCircle(sketch, "E13", {"center": v(-37.3, 8.73) * mm, "radius": 2.38 * mm});
            skCircle(sketch, "E14.1.0.0", {"center": v(-27.78, 8.73) * mm, "radius": 2.38 * mm});
            skCircle(sketch, "E14.2.0.0", {"center": v(-18.26, 8.73) * mm, "radius": 2.38 * mm});
            skCircle(sketch, "E14.3.0.0", {"center": v(-8.73, 8.73) * mm, "radius": 2.38 * mm});
            skCircle(sketch, "E14.4.0.0", {"center": v(0.8, 8.73) * mm, "radius": 2.38 * mm});
            skCircle(sketch, "E14.5.0.0", {"center": v(10.32, 8.73) * mm, "radius": 2.38 * mm});
            skCircle(sketch, "E14.6.0.0", {"center": v(19.84, 8.73) * mm, "radius": 2.38 * mm});
            skCircle(sketch, "E14.7.0.0", {"center": v(29.37, 8.73) * mm, "radius": 2.38 * mm});
            skLineSegment(sketch, "E14.direction1", {"start": v(-37.3, 8.73) * mm, "end": v(-27.78, 8.73) * mm, "construction": true});
            skSolve(sketch);
        }
        {
            var Q0;
            Q0=makeQuery(id+"F9.imprint","IMPRINT",FACE,{"disambiguationData":[TD([[makeQuery(id+"F9.imprint","IMPRINT",EDGE,{"derivedFrom":sQuery(id+"F9.wireOp",EDGE,"E13")}),1.0]])]});
            var Q1;
            Q1=makeQuery(id+"F9.imprint","IMPRINT",FACE,{"disambiguationData":[TD([[makeQuery(id+"F9.imprint","IMPRINT",EDGE,{"derivedFrom":sQuery(id+"F9.wireOp",EDGE,"E14.1.0.0")}),1.0]])]});
            var Q2;
            Q2=makeQuery(id+"F9.imprint","IMPRINT",FACE,{"disambiguationData":[TD([[makeQuery(id+"F9.imprint","IMPRINT",EDGE,{"derivedFrom":sQuery(id+"F9.wireOp",EDGE,"E14.2.0.0")}),1.0]])]});
            var Q3;
            Q3=makeQuery(id+"F9.imprint","IMPRINT",FACE,{"disambiguationData":[TD([[makeQuery(id+"F9.imprint","IMPRINT",EDGE,{"derivedFrom":sQuery(id+"F9.wireOp",EDGE,"E14.3.0.0")}),1.0]])]});
            var Q4;
            Q4=makeQuery(id+"F9.imprint","IMPRINT",FACE,{"disambiguationData":[TD([[makeQuery(id+"F9.imprint","IMPRINT",EDGE,{"derivedFrom":sQuery(id+"F9.wireOp",EDGE,"E14.4.0.0")}),1.0]])]});
            var Q5;
            Q5=makeQuery(id+"F9.imprint","IMPRINT",FACE,{"disambiguationData":[TD([[makeQuery(id+"F9.imprint","IMPRINT",EDGE,{"derivedFrom":sQuery(id+"F9.wireOp",EDGE,"E14.5.0.0")}),1.0]])]});
            var Q6;
            Q6=makeQuery(id+"F9.imprint","IMPRINT",FACE,{"disambiguationData":[TD([[makeQuery(id+"F9.imprint","IMPRINT",EDGE,{"derivedFrom":sQuery(id+"F9.wireOp",EDGE,"E14.6.0.0")}),1.0]])]});
            var Q7;
            Q7=makeQuery(id+"F9.imprint","IMPRINT",FACE,{"disambiguationData":[TD([[makeQuery(id+"F9.imprint","IMPRINT",EDGE,{"derivedFrom":sQuery(id+"F9.wireOp",EDGE,"E14.7.0.0")}),1.0]])]});
            extrude(context, id + "F10", {"entities" : qUnion([Q0, Q1, Q2, Q3, Q4, Q5, Q6, Q7]), "operationType" : NewBodyOperationType.REMOVE, "oppositeDirection" : true, "depth" : 25.4 * mm, "offsetDistance" : 25.4 * mm});
        }
        {
            var Q0;
            Q0=makeQuery(id+"F1.opExtrude","CAP_FACE",FACE,{"disambiguationData":[OSD([sQuery(id+"F0.wireOp",EDGE,"E0.bottom"),sQuery(id+"F0.wireOp",EDGE,"E0.top"),sQuery(id+"F0.wireOp",EDGE,"E0.left"),sQuery(id+"F0.wireOp",EDGE,"E0.right")])],"isStart":false});
            var sketch = newSketch(context, id + "F11", { "sketchPlane" : qUnion([Q0])});
            skLineSegment(sketch, "E15", {"start": v(-37.3, 8.73) * mm, "end": v(-37.3, -7.14) * mm, "construction": true});
            skCircle(sketch, "E16.cCircle", {"center": v(-37.3, -0.8) * mm, "radius": 2.38 * mm, "construction": true});
            skLineSegment(sketch, "E16.0", {"start": v(-38.68, 1.59) * mm, "end": v(-35.93, 1.59) * mm});
            skLineSegment(sketch, "E16.1", {"start": v(-35.93, 1.59) * mm, "end": v(-34.56, -0.8) * mm});
            skLineSegment(sketch, "E16.2", {"start": v(-34.56, -0.8) * mm, "end": v(-35.93, -3.18) * mm});
            skLineSegment(sketch, "E16.3", {"start": v(-35.93, -3.18) * mm, "end": v(-38.68, -3.18) * mm});
            skLineSegment(sketch, "E16.4", {"start": v(-38.68, -3.18) * mm, "end": v(-40.06, -0.8) * mm});
            skLineSegment(sketch, "E16.5", {"start": v(-40.06, -0.8) * mm, "end": v(-38.68, 1.59) * mm});
            skPoint(sketch, "E16.0.midPoint", {"position": v(-37.3, 1.59) * mm});
            skPoint(sketch, "E17.1.0.0", {"position": v(-27.78, 1.59) * mm});
            skCircle(sketch, "E17.1.0.1", {"center": v(-27.78, -0.8) * mm, "radius": 2.38 * mm, "construction": true});
            skLineSegment(sketch, "E17.1.0.2", {"start": v(-29.16, 1.59) * mm, "end": v(-26.4, 1.59) * mm});
            skLineSegment(sketch, "E17.1.0.3", {"start": v(-26.4, 1.59) * mm, "end": v(-25.03, -0.8) * mm});
            skLineSegment(sketch, "E17.1.0.4", {"start": v(-25.03, -0.8) * mm, "end": v(-26.4, -3.18) * mm});
            skLineSegment(sketch, "E17.1.0.5", {"start": v(-26.4, -3.18) * mm, "end": v(-29.16, -3.18) * mm});
            skLineSegment(sketch, "E17.1.0.6", {"start": v(-29.16, -3.18) * mm, "end": v(-30.53, -0.8) * mm});
            skLineSegment(sketch, "E17.1.0.7", {"start": v(-30.53, -0.8) * mm, "end": v(-29.16, 1.59) * mm});
            skPoint(sketch, "E17.2.0.0", {"position": v(-18.26, 1.59) * mm});
            skCircle(sketch, "E17.2.0.1", {"center": v(-18.26, -0.8) * mm, "radius": 2.38 * mm, "construction": true});
            skLineSegment(sketch, "E17.2.0.2", {"start": v(-19.63, 1.59) * mm, "end": v(-16.88, 1.59) * mm});
            skLineSegment(sketch, "E17.2.0.3", {"start": v(-16.88, 1.59) * mm, "end": v(-15.5, -0.8) * mm});
            skLineSegment(sketch, "E17.2.0.4", {"start": v(-15.5, -0.8) * mm, "end": v(-16.88, -3.18) * mm});
            skLineSegment(sketch, "E17.2.0.5", {"start": v(-16.88, -3.17) * mm, "end": v(-19.63, -3.17) * mm});
            skLineSegment(sketch, "E17.2.0.6", {"start": v(-19.63, -3.18) * mm, "end": v(-21, -0.8) * mm});
            skLineSegment(sketch, "E17.2.0.7", {"start": v(-21, -0.8) * mm, "end": v(-19.63, 1.59) * mm});
            skPoint(sketch, "E17.3.0.0", {"position": v(-8.73, 1.59) * mm});
            skCircle(sketch, "E17.3.0.1", {"center": v(-8.73, -0.8) * mm, "radius": 2.38 * mm, "construction": true});
            skLineSegment(sketch, "E17.3.0.2", {"start": v(-10.1, 1.59) * mm, "end": v(-7.36, 1.59) * mm});
            skLineSegment(sketch, "E17.3.0.3", {"start": v(-7.36, 1.59) * mm, "end": v(-5.98, -0.8) * mm});
            skLineSegment(sketch, "E17.3.0.4", {"start": v(-5.98, -0.8) * mm, "end": v(-7.36, -3.18) * mm});
            skLineSegment(sketch, "E17.3.0.5", {"start": v(-7.36, -3.17) * mm, "end": v(-10.1, -3.17) * mm});
            skLineSegment(sketch, "E17.3.0.6", {"start": v(-10.1, -3.18) * mm, "end": v(-11.48, -0.8) * mm});
            skLineSegment(sketch, "E17.3.0.7", {"start": v(-11.48, -0.8) * mm, "end": v(-10.1, 1.59) * mm});
            skPoint(sketch, "E17.4.0.0", {"position": v(0.8, 1.59) * mm});
            skCircle(sketch, "E17.4.0.1", {"center": v(0.8, -0.8) * mm, "radius": 2.38 * mm, "construction": true});
            skLineSegment(sketch, "E17.4.0.2", {"start": v(-0.58, 1.59) * mm, "end": v(2.17, 1.59) * mm});
            skLineSegment(sketch, "E17.4.0.3", {"start": v(2.17, 1.59) * mm, "end": v(3.54, -0.8) * mm});
            skLineSegment(sketch, "E17.4.0.4", {"start": v(3.54, -0.8) * mm, "end": v(2.17, -3.18) * mm});
            skLineSegment(sketch, "E17.4.0.5", {"start": v(2.17, -3.17) * mm, "end": v(-0.58, -3.17) * mm});
            skLineSegment(sketch, "E17.4.0.6", {"start": v(-0.58, -3.18) * mm, "end": v(-1.96, -0.8) * mm});
            skLineSegment(sketch, "E17.4.0.7", {"start": v(-1.96, -0.8) * mm, "end": v(-0.58, 1.59) * mm});
            skPoint(sketch, "E17.5.0.0", {"position": v(10.32, 1.59) * mm});
            skCircle(sketch, "E17.5.0.1", {"center": v(10.32, -0.8) * mm, "radius": 2.38 * mm, "construction": true});
            skLineSegment(sketch, "E17.5.0.2", {"start": v(8.94, 1.59) * mm, "end": v(11.7, 1.59) * mm});
            skLineSegment(sketch, "E17.5.0.3", {"start": v(11.7, 1.59) * mm, "end": v(13.07, -0.8) * mm});
            skLineSegment(sketch, "E17.5.0.4", {"start": v(13.07, -0.8) * mm, "end": v(11.7, -3.18) * mm});
            skLineSegment(sketch, "E17.5.0.5", {"start": v(11.7, -3.17) * mm, "end": v(8.94, -3.17) * mm});
            skLineSegment(sketch, "E17.5.0.6", {"start": v(8.94, -3.18) * mm, "end": v(7.57, -0.8) * mm});
            skLineSegment(sketch, "E17.5.0.7", {"start": v(7.57, -0.8) * mm, "end": v(8.94, 1.59) * mm});
            skPoint(sketch, "E17.6.0.0", {"position": v(19.84, 1.59) * mm});
            skCircle(sketch, "E17.6.0.1", {"center": v(19.84, -0.8) * mm, "radius": 2.38 * mm, "construction": true});
            skLineSegment(sketch, "E17.6.0.2", {"start": v(18.47, 1.59) * mm, "end": v(21.22, 1.59) * mm});
            skLineSegment(sketch, "E17.6.0.3", {"start": v(21.22, 1.59) * mm, "end": v(22.6, -0.8) * mm});
            skLineSegment(sketch, "E17.6.0.4", {"start": v(22.6, -0.8) * mm, "end": v(21.22, -3.18) * mm});
            skLineSegment(sketch, "E17.6.0.5", {"start": v(21.22, -3.17) * mm, "end": v(18.47, -3.17) * mm});
            skLineSegment(sketch, "E17.6.0.6", {"start": v(18.47, -3.18) * mm, "end": v(17.1, -0.8) * mm});
            skLineSegment(sketch, "E17.6.0.7", {"start": v(17.1, -0.8) * mm, "end": v(18.47, 1.59) * mm});
            skPoint(sketch, "E17.7.0.0", {"position": v(29.37, 1.59) * mm});
            skCircle(sketch, "E17.7.0.1", {"center": v(29.37, -0.8) * mm, "radius": 2.38 * mm, "construction": true});
            skLineSegment(sketch, "E17.7.0.2", {"start": v(28, 1.59) * mm, "end": v(30.74, 1.59) * mm});
            skLineSegment(sketch, "E17.7.0.3", {"start": v(30.74, 1.59) * mm, "end": v(32.12, -0.8) * mm});
            skLineSegment(sketch, "E17.7.0.4", {"start": v(32.12, -0.8) * mm, "end": v(30.74, -3.18) * mm});
            skLineSegment(sketch, "E17.7.0.5", {"start": v(30.74, -3.17) * mm, "end": v(28, -3.17) * mm});
            skLineSegment(sketch, "E17.7.0.6", {"start": v(28, -3.18) * mm, "end": v(26.62, -0.8) * mm});
            skLineSegment(sketch, "E17.7.0.7", {"start": v(26.62, -0.8) * mm, "end": v(28, 1.59) * mm});
            skLineSegment(sketch, "E17.direction1", {"start": v(-38.68, -3.18) * mm, "end": v(-29.16, -3.18) * mm, "construction": true});
            skSolve(sketch);
        }
        {
            var Q0;
            Q0=makeQuery(id+"F11.imprint","IMPRINT",FACE,{"disambiguationData":[TD([[makeQuery(id+"F11.imprint","IMPRINT",EDGE,{"derivedFrom":sQuery(id+"F11.wireOp",EDGE,"E16.0")}),-1.0]])]});
            var Q1;
            Q1=makeQuery(id+"F11.imprint","IMPRINT",FACE,{"disambiguationData":[TD([[makeQuery(id+"F11.imprint","IMPRINT",EDGE,{"derivedFrom":sQuery(id+"F11.wireOp",EDGE,"E17.1.0.2")}),-1.0]])]});
            var Q2;
            Q2=makeQuery(id+"F11.imprint","IMPRINT",FACE,{"disambiguationData":[TD([[makeQuery(id+"F11.imprint","IMPRINT",EDGE,{"derivedFrom":sQuery(id+"F11.wireOp",EDGE,"E17.2.0.2")}),-1.0]])]});
            var Q3;
            Q3=makeQuery(id+"F11.imprint","IMPRINT",FACE,{"disambiguationData":[TD([[makeQuery(id+"F11.imprint","IMPRINT",EDGE,{"derivedFrom":sQuery(id+"F11.wireOp",EDGE,"E17.3.0.2")}),-1.0]])]});
            var Q4;
            Q4=makeQuery(id+"F11.imprint","IMPRINT",FACE,{"disambiguationData":[TD([[makeQuery(id+"F11.imprint","IMPRINT",EDGE,{"derivedFrom":sQuery(id+"F11.wireOp",EDGE,"E17.4.0.2")}),-1.0]])]});
            var Q5;
            Q5=makeQuery(id+"F11.imprint","IMPRINT",FACE,{"disambiguationData":[TD([[makeQuery(id+"F11.imprint","IMPRINT",EDGE,{"derivedFrom":sQuery(id+"F11.wireOp",EDGE,"E17.5.0.2")}),-1.0]])]});
            var Q6;
            Q6=makeQuery(id+"F11.imprint","IMPRINT",FACE,{"disambiguationData":[TD([[makeQuery(id+"F11.imprint","IMPRINT",EDGE,{"derivedFrom":sQuery(id+"F11.wireOp",EDGE,"E17.6.0.2")}),-1.0]])]});
            var Q7;
            Q7=makeQuery(id+"F11.imprint","IMPRINT",FACE,{"disambiguationData":[TD([[makeQuery(id+"F11.imprint","IMPRINT",EDGE,{"derivedFrom":sQuery(id+"F11.wireOp",EDGE,"E17.7.0.2")}),-1.0]])]});
            extrude(context, id + "F12", {"entities" : qUnion([Q0, Q1, Q2, Q3, Q4, Q5, Q6, Q7]), "operationType" : NewBodyOperationType.REMOVE, "oppositeDirection" : true, "depth" : 25.4 * mm, "offsetDistance" : 25.4 * mm});
        }
        {
            var Q0;
            Q0=makeQuery(id+"F1.opExtrude","CAP_FACE",FACE,{"disambiguationData":[OSD([sQuery(id+"F0.wireOp",EDGE,"E0.bottom"),sQuery(id+"F0.wireOp",EDGE,"E0.top"),sQuery(id+"F0.wireOp",EDGE,"E0.left"),sQuery(id+"F0.wireOp",EDGE,"E0.right")])],"isStart":false});
            var sketch = newSketch(context, id + "F13", { "sketchPlane" : qUnion([Q0])});
            skLineSegment(sketch, "E18", {"start": v(-46.65, -10.32) * mm, "end": v(-28.9, -10.32) * mm, "construction": true});
            skCircle(sketch, "E19.cCircle", {"center": v(-36.3, -10.32) * mm, "radius": 1.37 * mm, "construction": true});
            skLineSegment(sketch, "E19.0", {"start": v(-34.92, -7.94) * mm, "end": v(-34.92, -12.7) * mm});
            skLineSegment(sketch, "E19.1", {"start": v(-34.92, -12.7) * mm, "end": v(-39.05, -10.32) * mm});
            skLineSegment(sketch, "E19.2", {"start": v(-39.05, -10.32) * mm, "end": v(-34.92, -7.94) * mm});
            skPoint(sketch, "E19.0.midPoint", {"position": v(-34.92, -10.32) * mm});
            skPoint(sketch, "E20.1.0.0", {"position": v(-25.4, -10.32) * mm});
            skLineSegment(sketch, "E20.1.0.1", {"start": v(-29.52, -10.32) * mm, "end": v(-25.4, -7.94) * mm});
            skLineSegment(sketch, "E20.1.0.2", {"start": v(-25.4, -12.7) * mm, "end": v(-29.52, -10.32) * mm});
            skLineSegment(sketch, "E20.1.0.3", {"start": v(-25.4, -7.94) * mm, "end": v(-25.4, -12.7) * mm});
            skCircle(sketch, "E20.1.0.4", {"center": v(-26.77, -10.32) * mm, "radius": 1.37 * mm, "construction": true});
            skPoint(sketch, "E20.2.0.0", {"position": v(-15.88, -10.32) * mm});
            skLineSegment(sketch, "E20.2.0.1", {"start": v(-20, -10.32) * mm, "end": v(-15.87, -7.94) * mm});
            skLineSegment(sketch, "E20.2.0.2", {"start": v(-15.87, -12.7) * mm, "end": v(-20, -10.32) * mm});
            skLineSegment(sketch, "E20.2.0.3", {"start": v(-15.87, -7.94) * mm, "end": v(-15.87, -12.7) * mm});
            skCircle(sketch, "E20.2.0.4", {"center": v(-17.25, -10.32) * mm, "radius": 1.37 * mm, "construction": true});
            skPoint(sketch, "E20.3.0.0", {"position": v(-6.35, -10.32) * mm});
            skLineSegment(sketch, "E20.3.0.1", {"start": v(-10.47, -10.32) * mm, "end": v(-6.35, -7.94) * mm});
            skLineSegment(sketch, "E20.3.0.2", {"start": v(-6.35, -12.7) * mm, "end": v(-10.47, -10.32) * mm});
            skLineSegment(sketch, "E20.3.0.3", {"start": v(-6.35, -7.94) * mm, "end": v(-6.35, -12.7) * mm});
            skCircle(sketch, "E20.3.0.4", {"center": v(-7.72, -10.32) * mm, "radius": 1.37 * mm, "construction": true});
            skPoint(sketch, "E20.4.0.0", {"position": v(3.17, -10.32) * mm});
            skLineSegment(sketch, "E20.4.0.1", {"start": v(-0.95, -10.32) * mm, "end": v(3.18, -7.94) * mm});
            skLineSegment(sketch, "E20.4.0.2", {"start": v(3.18, -12.7) * mm, "end": v(-0.95, -10.32) * mm});
            skLineSegment(sketch, "E20.4.0.3", {"start": v(3.18, -7.94) * mm, "end": v(3.18, -12.7) * mm});
            skCircle(sketch, "E20.4.0.4", {"center": v(1.8, -10.32) * mm, "radius": 1.37 * mm, "construction": true});
            skPoint(sketch, "E20.5.0.0", {"position": v(12.7, -10.32) * mm});
            skLineSegment(sketch, "E20.5.0.1", {"start": v(8.58, -10.32) * mm, "end": v(12.7, -7.94) * mm});
            skLineSegment(sketch, "E20.5.0.2", {"start": v(12.7, -12.7) * mm, "end": v(8.58, -10.32) * mm});
            skLineSegment(sketch, "E20.5.0.3", {"start": v(12.7, -7.94) * mm, "end": v(12.7, -12.7) * mm});
            skCircle(sketch, "E20.5.0.4", {"center": v(11.33, -10.32) * mm, "radius": 1.37 * mm, "construction": true});
            skPoint(sketch, "E20.6.0.0", {"position": v(22.22, -10.32) * mm});
            skLineSegment(sketch, "E20.6.0.1", {"start": v(18.1, -10.32) * mm, "end": v(22.23, -7.94) * mm});
            skLineSegment(sketch, "E20.6.0.2", {"start": v(22.23, -12.7) * mm, "end": v(18.1, -10.32) * mm});
            skLineSegment(sketch, "E20.6.0.3", {"start": v(22.22, -7.94) * mm, "end": v(22.22, -12.7) * mm});
            skCircle(sketch, "E20.6.0.4", {"center": v(20.85, -10.32) * mm, "radius": 1.37 * mm, "construction": true});
            skPoint(sketch, "E20.7.0.0", {"position": v(31.75, -10.32) * mm});
            skLineSegment(sketch, "E20.7.0.1", {"start": v(27.63, -10.32) * mm, "end": v(31.75, -7.94) * mm});
            skLineSegment(sketch, "E20.7.0.2", {"start": v(31.75, -12.7) * mm, "end": v(27.63, -10.32) * mm});
            skLineSegment(sketch, "E20.7.0.3", {"start": v(31.75, -7.94) * mm, "end": v(31.75, -12.7) * mm});
            skCircle(sketch, "E20.7.0.4", {"center": v(30.38, -10.32) * mm, "radius": 1.37 * mm, "construction": true});
            skLineSegment(sketch, "E20.direction1", {"start": v(-39.05, -10.32) * mm, "end": v(-29.52, -10.32) * mm, "construction": true});
            skLineSegment(sketch, "E21", {"start": v(-34.92, 18.54) * mm, "end": v(-34.92, -29.9) * mm, "construction": true});
            skSolve(sketch);
        }
        {
            var Q0;
            Q0=makeQuery(id+"F13.imprint","IMPRINT",FACE,{"disambiguationData":[TD([[makeQuery(id+"F13.imprint","IMPRINT",EDGE,{"derivedFrom":sQuery(id+"F13.wireOp",EDGE,"E19.0")}),-1.0]])]});
            var Q1;
            Q1=makeQuery(id+"F13.imprint","IMPRINT",FACE,{"disambiguationData":[TD([[makeQuery(id+"F13.imprint","IMPRINT",EDGE,{"derivedFrom":sQuery(id+"F13.wireOp",EDGE,"E20.1.0.1")}),-1.0]])]});
            var Q2;
            Q2=makeQuery(id+"F13.imprint","IMPRINT",FACE,{"disambiguationData":[TD([[makeQuery(id+"F13.imprint","IMPRINT",EDGE,{"derivedFrom":sQuery(id+"F13.wireOp",EDGE,"E20.2.0.1")}),-1.0]])]});
            var Q3;
            Q3=makeQuery(id+"F13.imprint","IMPRINT",FACE,{"disambiguationData":[TD([[makeQuery(id+"F13.imprint","IMPRINT",EDGE,{"derivedFrom":sQuery(id+"F13.wireOp",EDGE,"E20.3.0.1")}),-1.0]])]});
            var Q4;
            Q4=makeQuery(id+"F13.imprint","IMPRINT",FACE,{"disambiguationData":[TD([[makeQuery(id+"F13.imprint","IMPRINT",EDGE,{"derivedFrom":sQuery(id+"F13.wireOp",EDGE,"E20.4.0.1")}),-1.0]])]});
            var Q5;
            Q5=makeQuery(id+"F13.imprint","IMPRINT",FACE,{"disambiguationData":[TD([[makeQuery(id+"F13.imprint","IMPRINT",EDGE,{"derivedFrom":sQuery(id+"F13.wireOp",EDGE,"E20.5.0.1")}),-1.0]])]});
            var Q6;
            Q6=makeQuery(id+"F13.imprint","IMPRINT",FACE,{"disambiguationData":[TD([[makeQuery(id+"F13.imprint","IMPRINT",EDGE,{"derivedFrom":sQuery(id+"F13.wireOp",EDGE,"E20.6.0.1")}),-1.0]])]});
            var Q7;
            Q7=makeQuery(id+"F13.imprint","IMPRINT",FACE,{"disambiguationData":[TD([[makeQuery(id+"F13.imprint","IMPRINT",EDGE,{"derivedFrom":sQuery(id+"F13.wireOp",EDGE,"E20.7.0.1")}),-1.0]])]});
            extrude(context, id + "F14", {"entities" : qUnion([Q0, Q1, Q2, Q3, Q4, Q5, Q6, Q7]), "operationType" : NewBodyOperationType.REMOVE, "oppositeDirection" : true, "depth" : 25.4 * mm, "offsetDistance" : 25.4 * mm});
        }
        {
            var Q0;
            Q0=makeQuery(id+"F1.opExtrude","CAP_FACE",FACE,{"disambiguationData":[OSD([sQuery(id+"F0.wireOp",EDGE,"E0.bottom"),sQuery(id+"F0.wireOp",EDGE,"E0.top"),sQuery(id+"F0.wireOp",EDGE,"E0.left"),sQuery(id+"F0.wireOp",EDGE,"E0.right")])],"isStart":false});
            var sketch = newSketch(context, id + "F15", { "sketchPlane" : qUnion([Q0])});
            skLineSegment(sketch, "E22", {"start": v(-38.5, -21.03) * mm, "end": v(-38.5, -18.65) * mm, "construction": true});
            skLineSegment(sketch, "E23", {"start": v(-38.5, -19.84) * mm, "end": v(-34.92, -19.84) * mm, "construction": true});
            skArc(sketch, "E24", {"start": v(-38.5, -19.84) * mm, "mid": v(-39.63, -21.41) * mm, "end": v(-37.78, -21.99) * mm});
            skArc(sketch, "E25", {"start": v(-37.78, -17.7) * mm, "mid": v(-39.63, -18.28) * mm, "end": v(-38.5, -19.84) * mm});
            skLineSegment(sketch, "E26", {"start": v(-34.92, -19.84) * mm, "end": v(-37.78, -21.99) * mm});
            skLineSegment(sketch, "E27", {"start": v(-34.92, -19.84) * mm, "end": v(-37.78, -17.7) * mm});
            skLineSegment(sketch, "E28", {"start": v(-34.92, 15.88) * mm, "end": v(-34.92, -32.08) * mm, "construction": true});
            skLineSegment(sketch, "E29", {"start": v(-39.69, 15.88) * mm, "end": v(-39.69, -31.95) * mm, "construction": true});
            skArc(sketch, "E30.1.0.0", {"start": v(-28.97, -19.84) * mm, "mid": v(-30.1, -21.41) * mm, "end": v(-28.26, -21.99) * mm});
            skLineSegment(sketch, "E30.1.0.1", {"start": v(-25.4, -19.84) * mm, "end": v(-28.26, -21.99) * mm});
            skLineSegment(sketch, "E30.1.0.2", {"start": v(-25.4, -19.84) * mm, "end": v(-28.26, -17.7) * mm});
            skLineSegment(sketch, "E30.1.0.3", {"start": v(-28.97, -19.84) * mm, "end": v(-25.4, -19.84) * mm, "construction": true});
            skLineSegment(sketch, "E30.1.0.4", {"start": v(-28.97, -21.03) * mm, "end": v(-28.97, -18.65) * mm, "construction": true});
            skArc(sketch, "E30.1.0.5", {"start": v(-28.26, -17.7) * mm, "mid": v(-30.1, -18.28) * mm, "end": v(-28.97, -19.84) * mm});
            skArc(sketch, "E30.2.0.0", {"start": v(-19.45, -19.84) * mm, "mid": v(-20.58, -21.41) * mm, "end": v(-18.73, -21.99) * mm});
            skLineSegment(sketch, "E30.2.0.1", {"start": v(-15.87, -19.84) * mm, "end": v(-18.73, -21.99) * mm});
            skLineSegment(sketch, "E30.2.0.2", {"start": v(-15.87, -19.84) * mm, "end": v(-18.73, -17.7) * mm});
            skLineSegment(sketch, "E30.2.0.3", {"start": v(-19.45, -19.84) * mm, "end": v(-15.87, -19.84) * mm, "construction": true});
            skLineSegment(sketch, "E30.2.0.4", {"start": v(-19.45, -21.03) * mm, "end": v(-19.45, -18.65) * mm, "construction": true});
            skArc(sketch, "E30.2.0.5", {"start": v(-18.73, -17.7) * mm, "mid": v(-20.58, -18.28) * mm, "end": v(-19.45, -19.84) * mm});
            skArc(sketch, "E30.3.0.0", {"start": v(-9.92, -19.84) * mm, "mid": v(-11.05, -21.41) * mm, "end": v(-9.2, -21.99) * mm});
            skLineSegment(sketch, "E30.3.0.1", {"start": v(-6.35, -19.84) * mm, "end": v(-9.2, -21.99) * mm});
            skLineSegment(sketch, "E30.3.0.2", {"start": v(-6.35, -19.84) * mm, "end": v(-9.2, -17.7) * mm});
            skLineSegment(sketch, "E30.3.0.3", {"start": v(-9.92, -19.84) * mm, "end": v(-6.35, -19.84) * mm, "construction": true});
            skLineSegment(sketch, "E30.3.0.4", {"start": v(-9.92, -21.03) * mm, "end": v(-9.92, -18.65) * mm, "construction": true});
            skArc(sketch, "E30.3.0.5", {"start": v(-9.2, -17.7) * mm, "mid": v(-11.05, -18.28) * mm, "end": v(-9.92, -19.84) * mm});
            skArc(sketch, "E30.4.0.0", {"start": v(-0.4, -19.84) * mm, "mid": v(-1.53, -21.41) * mm, "end": v(0.32, -21.99) * mm});
            skLineSegment(sketch, "E30.4.0.1", {"start": v(3.18, -19.84) * mm, "end": v(0.32, -21.99) * mm});
            skLineSegment(sketch, "E30.4.0.2", {"start": v(3.18, -19.84) * mm, "end": v(0.32, -17.7) * mm});
            skLineSegment(sketch, "E30.4.0.3", {"start": v(-0.4, -19.84) * mm, "end": v(3.18, -19.84) * mm, "construction": true});
            skLineSegment(sketch, "E30.4.0.4", {"start": v(-0.4, -21.03) * mm, "end": v(-0.4, -18.65) * mm, "construction": true});
            skArc(sketch, "E30.4.0.5", {"start": v(0.32, -17.7) * mm, "mid": v(-1.53, -18.28) * mm, "end": v(-0.4, -19.84) * mm});
            skArc(sketch, "E30.5.0.0", {"start": v(9.13, -19.84) * mm, "mid": v(8, -21.41) * mm, "end": v(9.84, -21.99) * mm});
            skLineSegment(sketch, "E30.5.0.1", {"start": v(12.7, -19.84) * mm, "end": v(9.84, -21.99) * mm});
            skLineSegment(sketch, "E30.5.0.2", {"start": v(12.7, -19.84) * mm, "end": v(9.84, -17.7) * mm});
            skLineSegment(sketch, "E30.5.0.3", {"start": v(9.13, -19.84) * mm, "end": v(12.7, -19.84) * mm, "construction": true});
            skLineSegment(sketch, "E30.5.0.4", {"start": v(9.13, -21.03) * mm, "end": v(9.13, -18.65) * mm, "construction": true});
            skArc(sketch, "E30.5.0.5", {"start": v(9.84, -17.7) * mm, "mid": v(8, -18.28) * mm, "end": v(9.13, -19.84) * mm});
            skArc(sketch, "E30.6.0.0", {"start": v(18.65, -19.84) * mm, "mid": v(17.52, -21.41) * mm, "end": v(19.37, -21.99) * mm});
            skLineSegment(sketch, "E30.6.0.1", {"start": v(22.23, -19.84) * mm, "end": v(19.37, -21.99) * mm});
            skLineSegment(sketch, "E30.6.0.2", {"start": v(22.23, -19.84) * mm, "end": v(19.37, -17.7) * mm});
            skLineSegment(sketch, "E30.6.0.3", {"start": v(18.65, -19.84) * mm, "end": v(22.23, -19.84) * mm, "construction": true});
            skLineSegment(sketch, "E30.6.0.4", {"start": v(18.65, -21.03) * mm, "end": v(18.65, -18.65) * mm, "construction": true});
            skArc(sketch, "E30.6.0.5", {"start": v(19.37, -17.7) * mm, "mid": v(17.52, -18.28) * mm, "end": v(18.65, -19.84) * mm});
            skArc(sketch, "E30.7.0.0", {"start": v(28.18, -19.84) * mm, "mid": v(27.05, -21.41) * mm, "end": v(28.9, -21.99) * mm});
            skLineSegment(sketch, "E30.7.0.1", {"start": v(31.75, -19.84) * mm, "end": v(28.9, -21.99) * mm});
            skLineSegment(sketch, "E30.7.0.2", {"start": v(31.75, -19.84) * mm, "end": v(28.9, -17.7) * mm});
            skLineSegment(sketch, "E30.7.0.3", {"start": v(28.18, -19.84) * mm, "end": v(31.75, -19.84) * mm, "construction": true});
            skLineSegment(sketch, "E30.7.0.4", {"start": v(28.18, -21.03) * mm, "end": v(28.18, -18.65) * mm, "construction": true});
            skArc(sketch, "E30.7.0.5", {"start": v(28.9, -17.7) * mm, "mid": v(27.05, -18.28) * mm, "end": v(28.18, -19.84) * mm});
            skLineSegment(sketch, "E30.direction1", {"start": v(-37.78, -21.99) * mm, "end": v(-28.26, -21.99) * mm, "construction": true});
            skSolve(sketch);
        }
        {
            var Q0;
            Q0=makeQuery(id+"F15.imprint","IMPRINT",FACE,{"disambiguationData":[TD([[makeQuery(id+"F15.imprint","IMPRINT",EDGE,{"derivedFrom":sQuery(id+"F15.wireOp",EDGE,"E24")}),1.0]])]});
            var Q1;
            Q1=makeQuery(id+"F15.imprint","IMPRINT",FACE,{"disambiguationData":[TD([[makeQuery(id+"F15.imprint","IMPRINT",EDGE,{"derivedFrom":sQuery(id+"F15.wireOp",EDGE,"52f32b24-5f55-4429-a675-c4ff8d142001.1.0.0")}),1.0]])]});
            var Q2;
            Q2=makeQuery(id+"F15.imprint","IMPRINT",FACE,{"disambiguationData":[TD([[makeQuery(id+"F15.imprint","IMPRINT",EDGE,{"derivedFrom":sQuery(id+"F15.wireOp",EDGE,"52f32b24-5f55-4429-a675-c4ff8d142001.2.0.0")}),1.0]])]});
            var Q3;
            Q3=makeQuery(id+"F15.imprint","IMPRINT",FACE,{"disambiguationData":[TD([[makeQuery(id+"F15.imprint","IMPRINT",EDGE,{"derivedFrom":sQuery(id+"F15.wireOp",EDGE,"52f32b24-5f55-4429-a675-c4ff8d142001.3.0.0")}),1.0]])]});
            var Q4;
            Q4=makeQuery(id+"F15.imprint","IMPRINT",FACE,{"disambiguationData":[TD([[makeQuery(id+"F15.imprint","IMPRINT",EDGE,{"derivedFrom":sQuery(id+"F15.wireOp",EDGE,"52f32b24-5f55-4429-a675-c4ff8d142001.4.0.0")}),1.0]])]});
            var Q5;
            Q5=makeQuery(id+"F15.imprint","IMPRINT",FACE,{"disambiguationData":[TD([[makeQuery(id+"F15.imprint","IMPRINT",EDGE,{"derivedFrom":sQuery(id+"F15.wireOp",EDGE,"52f32b24-5f55-4429-a675-c4ff8d142001.5.0.0")}),1.0]])]});
            var Q6;
            Q6=makeQuery(id+"F15.imprint","IMPRINT",FACE,{"disambiguationData":[TD([[makeQuery(id+"F15.imprint","IMPRINT",EDGE,{"derivedFrom":sQuery(id+"F15.wireOp",EDGE,"52f32b24-5f55-4429-a675-c4ff8d142001.6.0.0")}),1.0]])]});
            var Q7;
            Q7=makeQuery(id+"F15.imprint","IMPRINT",FACE,{"disambiguationData":[TD([[makeQuery(id+"F15.imprint","IMPRINT",EDGE,{"derivedFrom":sQuery(id+"F15.wireOp",EDGE,"52f32b24-5f55-4429-a675-c4ff8d142001.7.0.0")}),1.0]])]});
            var Q8;
            Q8=makeQuery(id+"F15.imprint","IMPRINT",FACE,{"disambiguationData":[TD([[makeQuery(id+"F15.imprint","IMPRINT",EDGE,{"derivedFrom":sQuery(id+"F15.wireOp",EDGE,"E30.1.0.0")}),1.0]])]});
            var Q9;
            Q9=makeQuery(id+"F15.imprint","IMPRINT",FACE,{"disambiguationData":[TD([[makeQuery(id+"F15.imprint","IMPRINT",EDGE,{"derivedFrom":sQuery(id+"F15.wireOp",EDGE,"E30.2.0.0")}),1.0]])]});
            var Q10;
            Q10=makeQuery(id+"F15.imprint","IMPRINT",FACE,{"disambiguationData":[TD([[makeQuery(id+"F15.imprint","IMPRINT",EDGE,{"derivedFrom":sQuery(id+"F15.wireOp",EDGE,"E30.3.0.0")}),1.0]])]});
            var Q11;
            Q11=makeQuery(id+"F15.imprint","IMPRINT",FACE,{"disambiguationData":[TD([[makeQuery(id+"F15.imprint","IMPRINT",EDGE,{"derivedFrom":sQuery(id+"F15.wireOp",EDGE,"E30.4.0.0")}),1.0]])]});
            var Q12;
            Q12=makeQuery(id+"F15.imprint","IMPRINT",FACE,{"disambiguationData":[TD([[makeQuery(id+"F15.imprint","IMPRINT",EDGE,{"derivedFrom":sQuery(id+"F15.wireOp",EDGE,"E30.5.0.0")}),1.0]])]});
            var Q13;
            Q13=makeQuery(id+"F15.imprint","IMPRINT",FACE,{"disambiguationData":[TD([[makeQuery(id+"F15.imprint","IMPRINT",EDGE,{"derivedFrom":sQuery(id+"F15.wireOp",EDGE,"E30.6.0.0")}),1.0]])]});
            var Q14;
            Q14=makeQuery(id+"F15.imprint","IMPRINT",FACE,{"disambiguationData":[TD([[makeQuery(id+"F15.imprint","IMPRINT",EDGE,{"derivedFrom":sQuery(id+"F15.wireOp",EDGE,"E30.7.0.0")}),1.0]])]});
            extrude(context, id + "F16", {"entities" : qUnion([Q0, Q1, Q2, Q3, Q4, Q5, Q6, Q7, Q8, Q9, Q10, Q11, Q12, Q13, Q14]), "operationType" : NewBodyOperationType.REMOVE, "oppositeDirection" : true, "depth" : 25.4 * mm, "offsetDistance" : 25.4 * mm});
        }
        {
            var Q0;
            Q0=makeQuery(id+"F1.opExtrude","CAP_FACE",FACE,{"disambiguationData":[OSD([sQuery(id+"F0.wireOp",EDGE,"E0.bottom"),sQuery(id+"F0.wireOp",EDGE,"E0.top"),sQuery(id+"F0.wireOp",EDGE,"E0.left"),sQuery(id+"F0.wireOp",EDGE,"E0.right")])],"isStart":true});
            var sketch = newSketch(context, id + "F17", { "sketchPlane" : qUnion([Q0])});
            skLineSegment(sketch, "E31", {"start": v(-39.69, -20.64) * mm, "end": v(-54.82, -20.64) * mm, "construction": true});
            skCircle(sketch, "E32.cCircle", {"center": v(-42.86, -20.64) * mm, "radius": 0.8 * mm, "construction": true});
            skLineSegment(sketch, "E32.0", {"start": v(-43.66, -22.01) * mm, "end": v(-43.66, -19.26) * mm});
            skLineSegment(sketch, "E32.1", {"start": v(-43.66, -19.26) * mm, "end": v(-41.27, -20.64) * mm});
            skLineSegment(sketch, "E32.2", {"start": v(-41.27, -20.64) * mm, "end": v(-43.66, -22.01) * mm});
            skPoint(sketch, "E32.0.midPoint", {"position": v(-43.66, -20.64) * mm});
            skPoint(sketch, "E33.0.1.0", {"position": v(-43.66, -15.88) * mm});
            skLineSegment(sketch, "E33.0.1.1", {"start": v(-41.27, -15.88) * mm, "end": v(-43.66, -17.25) * mm});
            skLineSegment(sketch, "E33.0.1.2", {"start": v(-43.66, -14.5) * mm, "end": v(-41.27, -15.87) * mm});
            skLineSegment(sketch, "E33.0.1.3", {"start": v(-43.66, -17.25) * mm, "end": v(-43.66, -14.5) * mm});
            skCircle(sketch, "E33.0.1.4", {"center": v(-42.86, -15.88) * mm, "radius": 0.8 * mm, "construction": true});
            skPoint(sketch, "E33.0.2.0", {"position": v(-43.66, -11.11) * mm});
            skLineSegment(sketch, "E33.0.2.1", {"start": v(-41.27, -11.11) * mm, "end": v(-43.66, -12.49) * mm});
            skLineSegment(sketch, "E33.0.2.2", {"start": v(-43.66, -9.74) * mm, "end": v(-41.27, -11.11) * mm});
            skLineSegment(sketch, "E33.0.2.3", {"start": v(-43.66, -12.49) * mm, "end": v(-43.66, -9.74) * mm});
            skCircle(sketch, "E33.0.2.4", {"center": v(-42.86, -11.11) * mm, "radius": 0.8 * mm, "construction": true});
            skPoint(sketch, "E33.0.3.0", {"position": v(-43.66, -6.35) * mm});
            skLineSegment(sketch, "E33.0.3.1", {"start": v(-41.27, -6.35) * mm, "end": v(-43.66, -7.72) * mm});
            skLineSegment(sketch, "E33.0.3.2", {"start": v(-43.66, -4.98) * mm, "end": v(-41.27, -6.35) * mm});
            skLineSegment(sketch, "E33.0.3.3", {"start": v(-43.66, -7.72) * mm, "end": v(-43.66, -4.98) * mm});
            skCircle(sketch, "E33.0.3.4", {"center": v(-42.86, -6.35) * mm, "radius": 0.8 * mm, "construction": true});
            skPoint(sketch, "E33.0.4.0", {"position": v(-43.66, -1.59) * mm});
            skLineSegment(sketch, "E33.0.4.1", {"start": v(-41.27, -1.59) * mm, "end": v(-43.66, -2.96) * mm});
            skLineSegment(sketch, "E33.0.4.2", {"start": v(-43.66, -0.21) * mm, "end": v(-41.27, -1.59) * mm});
            skLineSegment(sketch, "E33.0.4.3", {"start": v(-43.66, -2.96) * mm, "end": v(-43.66, -0.21) * mm});
            skCircle(sketch, "E33.0.4.4", {"center": v(-42.86, -1.59) * mm, "radius": 0.8 * mm, "construction": true});
            skPoint(sketch, "E33.0.5.0", {"position": v(-43.66, 3.17) * mm});
            skLineSegment(sketch, "E33.0.5.1", {"start": v(-41.27, 3.17) * mm, "end": v(-43.66, 1.8) * mm});
            skLineSegment(sketch, "E33.0.5.2", {"start": v(-43.66, 4.55) * mm, "end": v(-41.27, 3.18) * mm});
            skLineSegment(sketch, "E33.0.5.3", {"start": v(-43.66, 1.8) * mm, "end": v(-43.66, 4.55) * mm});
            skCircle(sketch, "E33.0.5.4", {"center": v(-42.86, 3.17) * mm, "radius": 0.8 * mm, "construction": true});
            skPoint(sketch, "E33.0.6.0", {"position": v(-43.66, 7.94) * mm});
            skLineSegment(sketch, "E33.0.6.1", {"start": v(-41.27, 7.94) * mm, "end": v(-43.66, 6.56) * mm});
            skLineSegment(sketch, "E33.0.6.2", {"start": v(-43.66, 9.31) * mm, "end": v(-41.27, 7.94) * mm});
            skLineSegment(sketch, "E33.0.6.3", {"start": v(-43.66, 6.56) * mm, "end": v(-43.66, 9.31) * mm});
            skCircle(sketch, "E33.0.6.4", {"center": v(-42.86, 7.94) * mm, "radius": 0.8 * mm, "construction": true});
            skPoint(sketch, "E33.0.7.0", {"position": v(-43.66, 12.7) * mm});
            skLineSegment(sketch, "E33.0.7.1", {"start": v(-41.27, 12.7) * mm, "end": v(-43.66, 11.33) * mm});
            skLineSegment(sketch, "E33.0.7.2", {"start": v(-43.66, 14.07) * mm, "end": v(-41.27, 12.7) * mm});
            skLineSegment(sketch, "E33.0.7.3", {"start": v(-43.66, 11.33) * mm, "end": v(-43.66, 14.07) * mm});
            skCircle(sketch, "E33.0.7.4", {"center": v(-42.86, 12.7) * mm, "radius": 0.8 * mm, "construction": true});
            skPoint(sketch, "E33.0.8.0", {"position": v(-43.66, 17.46) * mm});
            skLineSegment(sketch, "E33.0.8.1", {"start": v(-41.27, 17.46) * mm, "end": v(-43.66, 16.09) * mm});
            skLineSegment(sketch, "E33.0.8.2", {"start": v(-43.66, 18.84) * mm, "end": v(-41.27, 17.46) * mm});
            skLineSegment(sketch, "E33.0.8.3", {"start": v(-43.66, 16.09) * mm, "end": v(-43.66, 18.84) * mm});
            skCircle(sketch, "E33.0.8.4", {"center": v(-42.86, 17.46) * mm, "radius": 0.8 * mm, "construction": true});
            skPoint(sketch, "E33.0.9.0", {"position": v(-43.66, 22.22) * mm});
            skLineSegment(sketch, "E33.0.9.1", {"start": v(-41.27, 22.22) * mm, "end": v(-43.66, 20.85) * mm});
            skLineSegment(sketch, "E33.0.9.2", {"start": v(-43.66, 23.6) * mm, "end": v(-41.27, 22.23) * mm});
            skLineSegment(sketch, "E33.0.9.3", {"start": v(-43.66, 20.85) * mm, "end": v(-43.66, 23.6) * mm});
            skCircle(sketch, "E33.0.9.4", {"center": v(-42.86, 22.22) * mm, "radius": 0.8 * mm, "construction": true});
            skLineSegment(sketch, "E33.direction1", {"start": v(-43.66, -22.01) * mm, "end": v(-18.26, -22.01) * mm, "construction": true});
            skLineSegment(sketch, "E33.direction2", {"start": v(-43.66, -22.01) * mm, "end": v(-43.66, -17.25) * mm, "construction": true});
            skSolve(sketch);
        }
        {
            var Q0;
            {var subQ0=sQuery(id+"F17.wireOp",EDGE,"E32.2");var subQ1=sQuery(id+"F17.wireOp",EDGE,"E32.1");var subQ2=makeQuery(id+"F17.imprint","INTERSECT",VERTEX,{"derivedFrom":[subQ1,subQ0]});Q0=makeQuery(id+"F17.imprint","IMPRINT",FACE,{"disambiguationData":[TD([[makeQuery(id+"F17.imprint","IMPRINT",EDGE,{"disambiguationData":[TD([[subQ2,1.0]])],"derivedFrom":subQ1}),-1.0]])]});}
            var Q1;
            {var subQ0=sQuery(id+"F17.wireOp",EDGE,"E33.0.1.2");var subQ1=sQuery(id+"F17.wireOp",EDGE,"E33.0.1.1");var subQ2=makeQuery(id+"F17.imprint","INTERSECT",VERTEX,{"derivedFrom":[subQ1,subQ0]});Q1=makeQuery(id+"F17.imprint","IMPRINT",FACE,{"disambiguationData":[TD([[makeQuery(id+"F17.imprint","IMPRINT",EDGE,{"disambiguationData":[TD([[subQ2,-1.0]])],"derivedFrom":subQ1}),-1.0]])]});}
            var Q2;
            {var subQ0=sQuery(id+"F17.wireOp",EDGE,"E33.0.2.2");var subQ1=sQuery(id+"F17.wireOp",EDGE,"E33.0.2.1");var subQ2=makeQuery(id+"F17.imprint","INTERSECT",VERTEX,{"derivedFrom":[subQ1,subQ0]});Q2=makeQuery(id+"F17.imprint","IMPRINT",FACE,{"disambiguationData":[TD([[makeQuery(id+"F17.imprint","IMPRINT",EDGE,{"disambiguationData":[TD([[subQ2,-1.0]])],"derivedFrom":subQ1}),-1.0]])]});}
            var Q3;
            {var subQ0=sQuery(id+"F17.wireOp",EDGE,"E33.0.3.2");var subQ1=sQuery(id+"F17.wireOp",EDGE,"E33.0.3.1");var subQ2=makeQuery(id+"F17.imprint","INTERSECT",VERTEX,{"derivedFrom":[subQ1,subQ0]});Q3=makeQuery(id+"F17.imprint","IMPRINT",FACE,{"disambiguationData":[TD([[makeQuery(id+"F17.imprint","IMPRINT",EDGE,{"disambiguationData":[TD([[subQ2,-1.0]])],"derivedFrom":subQ1}),-1.0]])]});}
            var Q4;
            {var subQ0=sQuery(id+"F17.wireOp",EDGE,"E33.0.4.2");var subQ1=sQuery(id+"F17.wireOp",EDGE,"E33.0.4.1");var subQ2=makeQuery(id+"F17.imprint","INTERSECT",VERTEX,{"derivedFrom":[subQ1,subQ0]});Q4=makeQuery(id+"F17.imprint","IMPRINT",FACE,{"disambiguationData":[TD([[makeQuery(id+"F17.imprint","IMPRINT",EDGE,{"disambiguationData":[TD([[subQ2,-1.0]])],"derivedFrom":subQ1}),-1.0]])]});}
            var Q5;
            {var subQ0=sQuery(id+"F17.wireOp",EDGE,"E33.0.5.2");var subQ1=sQuery(id+"F17.wireOp",EDGE,"E33.0.5.1");var subQ2=makeQuery(id+"F17.imprint","INTERSECT",VERTEX,{"derivedFrom":[subQ1,subQ0]});Q5=makeQuery(id+"F17.imprint","IMPRINT",FACE,{"disambiguationData":[TD([[makeQuery(id+"F17.imprint","IMPRINT",EDGE,{"disambiguationData":[TD([[subQ2,-1.0]])],"derivedFrom":subQ1}),-1.0]])]});}
            var Q6;
            {var subQ0=sQuery(id+"F17.wireOp",EDGE,"E33.0.6.2");var subQ1=sQuery(id+"F17.wireOp",EDGE,"E33.0.6.1");var subQ2=makeQuery(id+"F17.imprint","INTERSECT",VERTEX,{"derivedFrom":[subQ1,subQ0]});Q6=makeQuery(id+"F17.imprint","IMPRINT",FACE,{"disambiguationData":[TD([[makeQuery(id+"F17.imprint","IMPRINT",EDGE,{"disambiguationData":[TD([[subQ2,-1.0]])],"derivedFrom":subQ1}),-1.0]])]});}
            var Q7;
            {var subQ0=sQuery(id+"F17.wireOp",EDGE,"E33.0.7.2");var subQ1=sQuery(id+"F17.wireOp",EDGE,"E33.0.7.1");var subQ2=makeQuery(id+"F17.imprint","INTERSECT",VERTEX,{"derivedFrom":[subQ1,subQ0]});Q7=makeQuery(id+"F17.imprint","IMPRINT",FACE,{"disambiguationData":[TD([[makeQuery(id+"F17.imprint","IMPRINT",EDGE,{"disambiguationData":[TD([[subQ2,-1.0]])],"derivedFrom":subQ1}),-1.0]])]});}
            var Q8;
            {var subQ0=sQuery(id+"F17.wireOp",EDGE,"E33.0.8.2");var subQ1=sQuery(id+"F17.wireOp",EDGE,"E33.0.8.1");var subQ2=makeQuery(id+"F17.imprint","INTERSECT",VERTEX,{"derivedFrom":[subQ1,subQ0]});Q8=makeQuery(id+"F17.imprint","IMPRINT",FACE,{"disambiguationData":[TD([[makeQuery(id+"F17.imprint","IMPRINT",EDGE,{"disambiguationData":[TD([[subQ2,-1.0]])],"derivedFrom":subQ1}),-1.0]])]});}
            var Q9;
            {var subQ0=sQuery(id+"F17.wireOp",EDGE,"E33.0.9.2");var subQ1=sQuery(id+"F17.wireOp",EDGE,"E33.0.9.1");var subQ2=makeQuery(id+"F17.imprint","INTERSECT",VERTEX,{"derivedFrom":[subQ1,subQ0]});Q9=makeQuery(id+"F17.imprint","IMPRINT",FACE,{"disambiguationData":[TD([[makeQuery(id+"F17.imprint","IMPRINT",EDGE,{"disambiguationData":[TD([[subQ2,-1.0]])],"derivedFrom":subQ1}),-1.0]])]});}
            extrude(context, id + "F18", {"entities" : qUnion([Q0, Q1, Q2, Q3, Q4, Q5, Q6, Q7, Q8, Q9]), "operationType" : NewBodyOperationType.REMOVE, "oppositeDirection" : true, "depth" : 25.4 * mm, "offsetDistance" : 25.4 * mm});
        }
        {
            var Q0;
            Q0=makeQuery(id+"F1.opExtrude","CAP_FACE",FACE,{"disambiguationData":[OSD([sQuery(id+"F0.wireOp",EDGE,"E0.bottom"),sQuery(id+"F0.wireOp",EDGE,"E0.top"),sQuery(id+"F0.wireOp",EDGE,"E0.left"),sQuery(id+"F0.wireOp",EDGE,"E0.right")])],"isStart":false});
            var sketch = newSketch(context, id + "F19", { "sketchPlane" : qUnion([Q0])});
            skLineSegment(sketch, "E34.bottom", {"start": v(34.13, -24.6) * mm, "end": v(40.48, -24.6) * mm});
            skLineSegment(sketch, "E34.top", {"start": v(34.13, 24.6) * mm, "end": v(40.48, 24.6) * mm});
            skLineSegment(sketch, "E34.left", {"start": v(34.13, -24.6) * mm, "end": v(34.13, 24.6) * mm});
            skLineSegment(sketch, "E34.right", {"start": v(40.48, -24.6) * mm, "end": v(40.48, 24.6) * mm});
            skSolve(sketch);
        }
        {
            var Q0;
            Q0=makeQuery(id+"F19.imprint","IMPRINT",FACE,{"disambiguationData":[TD([[makeQuery(id+"F19.imprint","IMPRINT",EDGE,{"derivedFrom":sQuery(id+"F19.wireOp",EDGE,"E34.bottom")}),1.0]])]});
            extrude(context, id + "F20", {"entities" : qUnion([Q0]), "operationType" : NewBodyOperationType.REMOVE, "oppositeDirection" : true, "depth" : 0.4 * mm, "offsetDistance" : 25.4 * mm});
        }
        {
            var Q0;
            Q0=makeQuery(id+"F20.boolean.opBoolean","COPY",EDGE,{"derivedFrom":makeQuery(id+"F20.opExtrude","SWEPT_EDGE",EDGE,{"disambiguationData":[OSD([sQuery(id+"F19.wireOp",EDGE,"E34.bottom"),sQuery(id+"F19.wireOp",EDGE,"E34.left")])]})});
            var Q1;
            Q1=makeQuery(id+"F20.boolean.opBoolean","COPY",EDGE,{"derivedFrom":makeQuery(id+"F20.opExtrude","SWEPT_EDGE",EDGE,{"disambiguationData":[OSD([sQuery(id+"F19.wireOp",EDGE,"E34.bottom"),sQuery(id+"F19.wireOp",EDGE,"E34.right")])]})});
            var Q2;
            Q2=makeQuery(id+"F20.boolean.opBoolean","COPY",EDGE,{"derivedFrom":makeQuery(id+"F20.opExtrude","SWEPT_EDGE",EDGE,{"disambiguationData":[OSD([sQuery(id+"F19.wireOp",EDGE,"E34.top"),sQuery(id+"F19.wireOp",EDGE,"E34.right")])]})});
            var Q3;
            Q3=makeQuery(id+"F20.boolean.opBoolean","COPY",EDGE,{"derivedFrom":makeQuery(id+"F20.opExtrude","SWEPT_EDGE",EDGE,{"disambiguationData":[OSD([sQuery(id+"F19.wireOp",EDGE,"E34.top"),sQuery(id+"F19.wireOp",EDGE,"E34.left")])]})});
            fillet(context, id + "F21", {"entities" : qUnion([Q0, Q1, Q2, Q3]), "radius" : 1.59 * mm, "tangentPropagation" : true, "allowEdgeOverflow" : false});
        }
        {
            var Q0;
            Q0=makeQuery(id+"F20.boolean.opBoolean","COPY",FACE,{"derivedFrom":makeQuery(id+"F20.opExtrude","CAP_FACE",FACE,{"disambiguationData":[OSD([sQuery(id+"F19.wireOp",EDGE,"E34.bottom"),sQuery(id+"F19.wireOp",EDGE,"E34.top"),sQuery(id+"F19.wireOp",EDGE,"E34.left"),sQuery(id+"F19.wireOp",EDGE,"E34.right")])],"isStart":false})});
            var sketch = newSketch(context, id + "F22", { "sketchPlane" : qUnion([Q0])});
            skText(sketch, "E35", { "text": "PORTER PIECES", "fontName": "OpenSans-Bold.ttf"});
            const initialGuessF22  = {"E35": [0.03976, -0.02381, 0, 1, 0.00461]};
            skSetInitialGuess(sketch, initialGuessF22);
            skSolve(sketch);
        }
        {
            var Q0;
            Q0=makeQuery(id+"F22.imprint","IMPRINT",FACE,{"disambiguationData":[TD([[makeQuery(id+"F22.imprint","IMPRINT",EDGE,{"derivedFrom":sQuery(id+"F22.wireOp",EDGE,"E35.sketch_text.stroke-0")}),-1.0]])]});
            var Q1;
            Q1=makeQuery(id+"F22.imprint","IMPRINT",FACE,{"disambiguationData":[TD([[makeQuery(id+"F22.imprint","IMPRINT",EDGE,{"derivedFrom":sQuery(id+"F22.wireOp",EDGE,"E35.sketch_text.stroke-16")}),-1.0]])]});
            var Q2;
            Q2=makeQuery(id+"F22.imprint","IMPRINT",FACE,{"disambiguationData":[TD([[makeQuery(id+"F22.imprint","IMPRINT",EDGE,{"derivedFrom":sQuery(id+"F22.wireOp",EDGE,"E35.sketch_text.stroke-30")}),-1.0]])]});
            var Q3;
            Q3=makeQuery(id+"F22.imprint","IMPRINT",FACE,{"disambiguationData":[TD([[makeQuery(id+"F22.imprint","IMPRINT",EDGE,{"derivedFrom":sQuery(id+"F22.wireOp",EDGE,"E35.sketch_text.stroke-49")}),-1.0]])]});
            var Q4;
            Q4=makeQuery(id+"F22.imprint","IMPRINT",FACE,{"disambiguationData":[TD([[makeQuery(id+"F22.imprint","IMPRINT",EDGE,{"derivedFrom":sQuery(id+"F22.wireOp",EDGE,"E35.sketch_text.stroke-57")}),-1.0]])]});
            var Q5;
            Q5=makeQuery(id+"F22.imprint","IMPRINT",FACE,{"disambiguationData":[TD([[makeQuery(id+"F22.imprint","IMPRINT",EDGE,{"derivedFrom":sQuery(id+"F22.wireOp",EDGE,"E35.sketch_text.stroke-69")}),-1.0]])]});
            var Q6;
            Q6=makeQuery(id+"F22.imprint","IMPRINT",FACE,{"disambiguationData":[TD([[makeQuery(id+"F22.imprint","IMPRINT",EDGE,{"derivedFrom":sQuery(id+"F22.wireOp",EDGE,"E35.sketch_text.stroke-88")}),-1.0]])]});
            var Q7;
            Q7=makeQuery(id+"F22.imprint","IMPRINT",FACE,{"disambiguationData":[TD([[makeQuery(id+"F22.imprint","IMPRINT",EDGE,{"derivedFrom":sQuery(id+"F22.wireOp",EDGE,"E35.sketch_text.stroke-104")}),-1.0]])]});
            var Q8;
            Q8=makeQuery(id+"F22.imprint","IMPRINT",FACE,{"disambiguationData":[TD([[makeQuery(id+"F22.imprint","IMPRINT",EDGE,{"derivedFrom":sQuery(id+"F22.wireOp",EDGE,"E35.sketch_text.stroke-108")}),-1.0]])]});
            var Q9;
            Q9=makeQuery(id+"F22.imprint","IMPRINT",FACE,{"disambiguationData":[TD([[makeQuery(id+"F22.imprint","IMPRINT",EDGE,{"derivedFrom":sQuery(id+"F22.wireOp",EDGE,"E35.sketch_text.stroke-120")}),-1.0]])]});
            var Q10;
            Q10=makeQuery(id+"F22.imprint","IMPRINT",FACE,{"disambiguationData":[TD([[makeQuery(id+"F22.imprint","IMPRINT",EDGE,{"derivedFrom":sQuery(id+"F22.wireOp",EDGE,"E35.sketch_text.stroke-135")}),-1.0]])]});
            var Q11;
            Q11=makeQuery(id+"F22.imprint","IMPRINT",FACE,{"disambiguationData":[TD([[makeQuery(id+"F22.imprint","IMPRINT",EDGE,{"derivedFrom":sQuery(id+"F22.wireOp",EDGE,"E35.sketch_text.stroke-147")}),-1.0]])]});
            extrude(context, id + "F23", {"entities" : qUnion([Q0, Q1, Q2, Q3, Q4, Q5, Q6, Q7, Q8, Q9, Q10, Q11]), "operationType" : NewBodyOperationType.ADD, "depth" : 0.4 * mm, "offsetDistance" : 25.4 * mm});
        }
        {
            var Q0;
            Q0=makeQuery(id+"F1.opExtrude","CAP_FACE",FACE,{"disambiguationData":[OSD([sQuery(id+"F0.wireOp",EDGE,"E0.bottom"),sQuery(id+"F0.wireOp",EDGE,"E0.top"),sQuery(id+"F0.wireOp",EDGE,"E0.left"),sQuery(id+"F0.wireOp",EDGE,"E0.right")])],"isStart":false});
            var sketch = newSketch(context, id + "F24", { "sketchPlane" : qUnion([Q0])});
            skLineSegment(sketch, "E36.0", {"start": v(-34.54, -13.36) * mm, "end": v(-39.81, -10.32) * mm});
            skLineSegment(sketch, "E37.0", {"start": v(-39.81, -10.32) * mm, "end": v(-34.54, -7.28) * mm});
            skArc(sketch, "E38.0", {"start": v(-41.28, 33.34) * mm, "mid": v(-46.89, 31.01) * mm, "end": v(-49.21, 25.4) * mm});
            skLineSegment(sketch, "E38.1", {"start": v(-36.94, 33.34) * mm, "end": v(-41.28, 33.34) * mm});
            skLineSegment(sketch, "E38.2", {"start": v(-32.18, 33.34) * mm, "end": v(-36.94, 33.34) * mm});
            skLineSegment(sketch, "E38.3", {"start": v(-27.41, 33.34) * mm, "end": v(-32.18, 33.34) * mm});
            skLineSegment(sketch, "E38.4", {"start": v(-22.65, 33.34) * mm, "end": v(-27.41, 33.34) * mm});
            skLineSegment(sketch, "E38.5", {"start": v(-17.89, 33.34) * mm, "end": v(-22.65, 33.34) * mm});
            skLineSegment(sketch, "E38.6", {"start": v(-13.13, 33.34) * mm, "end": v(-17.89, 33.34) * mm});
            skLineSegment(sketch, "E38.7", {"start": v(-8.36, 33.34) * mm, "end": v(-13.13, 33.34) * mm});
            skLineSegment(sketch, "E38.8", {"start": v(-3.6, 33.34) * mm, "end": v(-8.36, 33.34) * mm});
            skLineSegment(sketch, "E38.9", {"start": v(1.16, 33.34) * mm, "end": v(-3.6, 33.34) * mm});
            skLineSegment(sketch, "E38.10", {"start": v(5.92, 33.34) * mm, "end": v(1.16, 33.34) * mm});
            skLineSegment(sketch, "E38.11", {"start": v(-49.21, -19.48) * mm, "end": v(-49.21, -25.4) * mm});
            skLineSegment(sketch, "E38.12", {"start": v(-49.21, -14.71) * mm, "end": v(-49.21, -19.48) * mm});
            skLineSegment(sketch, "E38.13", {"start": v(-49.21, -9.95) * mm, "end": v(-49.21, -14.71) * mm});
            skLineSegment(sketch, "E38.14", {"start": v(-49.21, -5.19) * mm, "end": v(-49.21, -9.95) * mm});
            skLineSegment(sketch, "E38.15", {"start": v(-49.21, -0.43) * mm, "end": v(-49.21, -5.19) * mm});
            skLineSegment(sketch, "E38.16", {"start": v(-49.21, 4.34) * mm, "end": v(-49.21, -0.43) * mm});
            skLineSegment(sketch, "E38.17", {"start": v(-49.21, 23.39) * mm, "end": v(-49.21, 18.62) * mm});
            skLineSegment(sketch, "E38.18", {"start": v(-49.21, 18.62) * mm, "end": v(-49.21, 13.86) * mm});
            skLineSegment(sketch, "E38.19", {"start": v(-49.21, 13.86) * mm, "end": v(-49.21, 9.1) * mm});
            skLineSegment(sketch, "E38.20", {"start": v(-49.21, 9.1) * mm, "end": v(-49.21, 4.34) * mm});
            skArc(sketch, "E38.21", {"start": v(-49.21, -25.4) * mm, "mid": v(-46.89, -31.01) * mm, "end": v(-41.27, -33.34) * mm});
            skLineSegment(sketch, "E38.22", {"start": v(-41.27, -33.34) * mm, "end": v(41.28, -33.34) * mm});
            skArc(sketch, "E38.23", {"start": v(41.28, -33.34) * mm, "mid": v(46.89, -31.01) * mm, "end": v(49.21, -25.4) * mm});
            skLineSegment(sketch, "E38.24", {"start": v(49.21, -25.4) * mm, "end": v(49.21, 25.4) * mm});
            skArc(sketch, "E38.25", {"start": v(49.21, 25.4) * mm, "mid": v(46.89, 31.01) * mm, "end": v(41.27, 33.34) * mm});
            skLineSegment(sketch, "E38.26", {"start": v(41.27, 33.34) * mm, "end": v(34.5, 33.34) * mm});
            skLineSegment(sketch, "E38.27", {"start": v(34.5, 33.34) * mm, "end": v(29.74, 33.34) * mm});
            skLineSegment(sketch, "E38.28", {"start": v(29.74, 33.34) * mm, "end": v(24.97, 33.34) * mm});
            skLineSegment(sketch, "E38.29", {"start": v(24.97, 33.34) * mm, "end": v(20.21, 33.34) * mm});
            skLineSegment(sketch, "E38.30", {"start": v(20.21, 33.34) * mm, "end": v(15.45, 33.34) * mm});
            skLineSegment(sketch, "E38.31", {"start": v(15.45, 33.34) * mm, "end": v(10.69, 33.34) * mm});
            skLineSegment(sketch, "E38.32", {"start": v(-49.21, 25.4) * mm, "end": v(-49.21, 23.39) * mm});
            skLineSegment(sketch, "E38.33", {"start": v(10.69, 33.34) * mm, "end": v(5.92, 33.34) * mm});
            skLineSegment(sketch, "E39.0", {"start": v(-34.54, -7.28) * mm, "end": v(-34.54, -13.36) * mm});
            skLineSegment(sketch, "E40.1.0.0", {"start": v(-25.02, -7.28) * mm, "end": v(-25.02, -13.36) * mm});
            skLineSegment(sketch, "E40.1.0.1", {"start": v(-30.29, -10.32) * mm, "end": v(-25.02, -7.28) * mm});
            skLineSegment(sketch, "E40.1.0.2", {"start": v(-25.02, -13.36) * mm, "end": v(-30.29, -10.32) * mm});
            skLineSegment(sketch, "E40.2.0.0", {"start": v(-15.5, -7.28) * mm, "end": v(-15.5, -13.36) * mm});
            skLineSegment(sketch, "E40.2.0.1", {"start": v(-20.76, -10.32) * mm, "end": v(-15.5, -7.28) * mm});
            skLineSegment(sketch, "E40.2.0.2", {"start": v(-15.5, -13.36) * mm, "end": v(-20.76, -10.32) * mm});
            skLineSegment(sketch, "E40.3.0.0", {"start": v(-5.97, -7.28) * mm, "end": v(-5.97, -13.36) * mm});
            skLineSegment(sketch, "E40.3.0.1", {"start": v(-11.24, -10.32) * mm, "end": v(-5.97, -7.28) * mm});
            skLineSegment(sketch, "E40.3.0.2", {"start": v(-5.97, -13.36) * mm, "end": v(-11.24, -10.32) * mm});
            skLineSegment(sketch, "E40.4.0.0", {"start": v(3.56, -7.28) * mm, "end": v(3.56, -13.36) * mm});
            skLineSegment(sketch, "E40.4.0.1", {"start": v(-1.71, -10.32) * mm, "end": v(3.56, -7.28) * mm});
            skLineSegment(sketch, "E40.4.0.2", {"start": v(3.56, -13.36) * mm, "end": v(-1.71, -10.32) * mm});
            skLineSegment(sketch, "E40.5.0.0", {"start": v(13.08, -7.28) * mm, "end": v(13.08, -13.36) * mm});
            skLineSegment(sketch, "E40.5.0.1", {"start": v(7.81, -10.32) * mm, "end": v(13.08, -7.28) * mm});
            skLineSegment(sketch, "E40.5.0.2", {"start": v(13.08, -13.36) * mm, "end": v(7.81, -10.32) * mm});
            skLineSegment(sketch, "E40.6.0.0", {"start": v(22.6, -7.28) * mm, "end": v(22.6, -13.36) * mm});
            skLineSegment(sketch, "E40.6.0.1", {"start": v(17.34, -10.32) * mm, "end": v(22.6, -7.28) * mm});
            skLineSegment(sketch, "E40.6.0.2", {"start": v(22.6, -13.36) * mm, "end": v(17.34, -10.32) * mm});
            skLineSegment(sketch, "E40.7.0.0", {"start": v(32.13, -7.28) * mm, "end": v(32.13, -13.36) * mm});
            skLineSegment(sketch, "E40.7.0.1", {"start": v(26.86, -10.32) * mm, "end": v(32.13, -7.28) * mm});
            skLineSegment(sketch, "E40.7.0.2", {"start": v(32.13, -13.36) * mm, "end": v(26.86, -10.32) * mm});
            skLineSegment(sketch, "E40.direction1", {"start": v(-39.81, -10.32) * mm, "end": v(-30.29, -10.32) * mm, "construction": true});
            skSolve(sketch);
        }
        {
            var Q0;
            Q0=makeQuery(id+"F24.imprint","IMPRINT",FACE,{"disambiguationData":[TD([[makeQuery(id+"F24.imprint","IMPRINT",EDGE,{"derivedFrom":sQuery(id+"F24.wireOp",EDGE,"E36.0")}),-1.0]])]});
            var Q1;
            Q1=makeQuery(id+"F24.imprint","IMPRINT",FACE,{"disambiguationData":[TD([[makeQuery(id+"F24.imprint","IMPRINT",EDGE,{"derivedFrom":sQuery(id+"F24.wireOp",EDGE,"E40.1.0.0")}),-1.0]])]});
            var Q2;
            Q2=makeQuery(id+"F24.imprint","IMPRINT",FACE,{"disambiguationData":[TD([[makeQuery(id+"F24.imprint","IMPRINT",EDGE,{"derivedFrom":sQuery(id+"F24.wireOp",EDGE,"E40.2.0.0")}),-1.0]])]});
            var Q3;
            Q3=makeQuery(id+"F24.imprint","IMPRINT",FACE,{"disambiguationData":[TD([[makeQuery(id+"F24.imprint","IMPRINT",EDGE,{"derivedFrom":sQuery(id+"F24.wireOp",EDGE,"E40.3.0.0")}),-1.0]])]});
            var Q4;
            Q4=makeQuery(id+"F24.imprint","IMPRINT",FACE,{"disambiguationData":[TD([[makeQuery(id+"F24.imprint","IMPRINT",EDGE,{"derivedFrom":sQuery(id+"F24.wireOp",EDGE,"E40.4.0.0")}),-1.0]])]});
            var Q5;
            Q5=makeQuery(id+"F24.imprint","IMPRINT",FACE,{"disambiguationData":[TD([[makeQuery(id+"F24.imprint","IMPRINT",EDGE,{"derivedFrom":sQuery(id+"F24.wireOp",EDGE,"E40.5.0.0")}),-1.0]])]});
            var Q6;
            Q6=makeQuery(id+"F24.imprint","IMPRINT",FACE,{"disambiguationData":[TD([[makeQuery(id+"F24.imprint","IMPRINT",EDGE,{"derivedFrom":sQuery(id+"F24.wireOp",EDGE,"E40.6.0.0")}),-1.0]])]});
            var Q7;
            Q7=makeQuery(id+"F24.imprint","IMPRINT",FACE,{"disambiguationData":[TD([[makeQuery(id+"F24.imprint","IMPRINT",EDGE,{"derivedFrom":sQuery(id+"F24.wireOp",EDGE,"E40.7.0.0")}),-1.0]])]});
            extrude(context, id + "F25", {"entities" : qUnion([Q0, Q1, Q2, Q3, Q4, Q5, Q6, Q7]), "operationType" : NewBodyOperationType.REMOVE, "oppositeDirection" : true, "depth" : 25.4 * mm, "offsetDistance" : 25.4 * mm});
        }
        {
            var Q0;
            Q0=makeQuery(id+"F1.opExtrude","CAP_FACE",FACE,{"disambiguationData":[OSD([sQuery(id+"F0.wireOp",EDGE,"E0.bottom"),sQuery(id+"F0.wireOp",EDGE,"E0.top"),sQuery(id+"F0.wireOp",EDGE,"E0.left"),sQuery(id+"F0.wireOp",EDGE,"E0.right")])],"isStart":false});
            var sketch = newSketch(context, id + "F26", { "sketchPlane" : qUnion([Q0])});
            skLineSegment(sketch, "E41.0", {"start": v(-34.29, -19.84) * mm, "end": v(-37.55, -17.4) * mm});
            skArc(sketch, "E42.0", {"start": v(-37.55, -17.4) * mm, "mid": v(-39.72, -17.67) * mm, "end": v(-39.52, -19.84) * mm});
            skArc(sketch, "E43.0", {"start": v(-39.52, -19.84) * mm, "mid": v(-39.72, -22.02) * mm, "end": v(-37.55, -22.3) * mm});
            skLineSegment(sketch, "E44.0", {"start": v(-34.29, -19.84) * mm, "end": v(-37.55, -22.3) * mm});
            skLineSegment(sketch, "E45.1.0.0", {"start": v(-24.76, -19.84) * mm, "end": v(-28.03, -22.3) * mm});
            skArc(sketch, "E45.1.0.1", {"start": v(-30, -19.84) * mm, "mid": v(-30.2, -22.02) * mm, "end": v(-28.03, -22.3) * mm});
            skLineSegment(sketch, "E45.1.0.2", {"start": v(-24.76, -19.84) * mm, "end": v(-28.03, -17.4) * mm});
            skArc(sketch, "E45.1.0.3", {"start": v(-28.03, -17.4) * mm, "mid": v(-30.2, -17.67) * mm, "end": v(-30, -19.84) * mm});
            skLineSegment(sketch, "E45.2.0.0", {"start": v(-15.24, -19.84) * mm, "end": v(-18.5, -22.3) * mm});
            skArc(sketch, "E45.2.0.1", {"start": v(-20.47, -19.84) * mm, "mid": v(-20.67, -22.02) * mm, "end": v(-18.5, -22.3) * mm});
            skLineSegment(sketch, "E45.2.0.2", {"start": v(-15.24, -19.84) * mm, "end": v(-18.5, -17.4) * mm});
            skArc(sketch, "E45.2.0.3", {"start": v(-18.5, -17.4) * mm, "mid": v(-20.67, -17.67) * mm, "end": v(-20.47, -19.84) * mm});
            skLineSegment(sketch, "E45.3.0.0", {"start": v(-5.71, -19.84) * mm, "end": v(-8.98, -22.3) * mm});
            skArc(sketch, "E45.3.0.1", {"start": v(-10.95, -19.84) * mm, "mid": v(-11.15, -22.02) * mm, "end": v(-8.98, -22.3) * mm});
            skLineSegment(sketch, "E45.3.0.2", {"start": v(-5.71, -19.84) * mm, "end": v(-8.98, -17.4) * mm});
            skArc(sketch, "E45.3.0.3", {"start": v(-8.98, -17.4) * mm, "mid": v(-11.15, -17.67) * mm, "end": v(-10.95, -19.84) * mm});
            skLineSegment(sketch, "E45.4.0.0", {"start": v(3.81, -19.84) * mm, "end": v(0.55, -22.3) * mm});
            skArc(sketch, "E45.4.0.1", {"start": v(-1.42, -19.84) * mm, "mid": v(-1.62, -22.02) * mm, "end": v(0.55, -22.3) * mm});
            skLineSegment(sketch, "E45.4.0.2", {"start": v(3.81, -19.84) * mm, "end": v(0.55, -17.4) * mm});
            skArc(sketch, "E45.4.0.3", {"start": v(0.55, -17.4) * mm, "mid": v(-1.62, -17.67) * mm, "end": v(-1.42, -19.84) * mm});
            skLineSegment(sketch, "E45.5.0.0", {"start": v(13.34, -19.84) * mm, "end": v(10.07, -22.3) * mm});
            skArc(sketch, "E45.5.0.1", {"start": v(8.1, -19.84) * mm, "mid": v(7.9, -22.02) * mm, "end": v(10.07, -22.3) * mm});
            skLineSegment(sketch, "E45.5.0.2", {"start": v(13.34, -19.84) * mm, "end": v(10.07, -17.4) * mm});
            skArc(sketch, "E45.5.0.3", {"start": v(10.07, -17.4) * mm, "mid": v(7.9, -17.67) * mm, "end": v(8.1, -19.84) * mm});
            skLineSegment(sketch, "E45.6.0.0", {"start": v(22.86, -19.84) * mm, "end": v(19.6, -22.3) * mm});
            skArc(sketch, "E45.6.0.1", {"start": v(17.63, -19.84) * mm, "mid": v(17.43, -22.02) * mm, "end": v(19.6, -22.3) * mm});
            skLineSegment(sketch, "E45.6.0.2", {"start": v(22.86, -19.84) * mm, "end": v(19.6, -17.4) * mm});
            skArc(sketch, "E45.6.0.3", {"start": v(19.6, -17.4) * mm, "mid": v(17.43, -17.67) * mm, "end": v(17.63, -19.84) * mm});
            skLineSegment(sketch, "E45.7.0.0", {"start": v(32.39, -19.84) * mm, "end": v(29.12, -22.3) * mm});
            skArc(sketch, "E45.7.0.1", {"start": v(27.15, -19.84) * mm, "mid": v(26.95, -22.02) * mm, "end": v(29.12, -22.3) * mm});
            skLineSegment(sketch, "E45.7.0.2", {"start": v(32.39, -19.84) * mm, "end": v(29.12, -17.4) * mm});
            skArc(sketch, "E45.7.0.3", {"start": v(29.12, -17.4) * mm, "mid": v(26.95, -17.67) * mm, "end": v(27.15, -19.84) * mm});
            skLineSegment(sketch, "E45.direction1", {"start": v(-37.55, -22.3) * mm, "end": v(-28.03, -22.3) * mm, "construction": true});
            skPoint(sketch, "E46.orphan", {"position": v(-36.54, -18.16) * mm});
            skPoint(sketch, "E47.orphan", {"position": v(-27.01, -18.16) * mm});
            skPoint(sketch, "E48.orphan", {"position": v(-17.49, -18.16) * mm});
            skPoint(sketch, "E49.orphan", {"position": v(-7.96, -18.16) * mm});
            skPoint(sketch, "E50.orphan", {"position": v(1.56, -18.16) * mm});
            skPoint(sketch, "E51.orphan", {"position": v(11.09, -18.16) * mm});
            skPoint(sketch, "E52.orphan", {"position": v(30.14, -18.16) * mm});
            skPoint(sketch, "E53.orphan", {"position": v(20.61, -18.16) * mm});
            skSolve(sketch);
        }
        {
            var Q0;
            Q0=makeQuery(id+"F26.imprint","IMPRINT",FACE,{"disambiguationData":[TD([[makeQuery(id+"F26.imprint","IMPRINT",EDGE,{"derivedFrom":sQuery(id+"F26.wireOp",EDGE,"E41.0")}),1.0]])]});
            var Q1;
            Q1=makeQuery(id+"F26.imprint","IMPRINT",FACE,{"disambiguationData":[TD([[makeQuery(id+"F26.imprint","IMPRINT",EDGE,{"derivedFrom":sQuery(id+"F26.wireOp",EDGE,"E45.1.0.0")}),-1.0]])]});
            var Q2;
            Q2=makeQuery(id+"F26.imprint","IMPRINT",FACE,{"disambiguationData":[TD([[makeQuery(id+"F26.imprint","IMPRINT",EDGE,{"derivedFrom":sQuery(id+"F26.wireOp",EDGE,"E45.2.0.0")}),-1.0]])]});
            var Q3;
            Q3=makeQuery(id+"F26.imprint","IMPRINT",FACE,{"disambiguationData":[TD([[makeQuery(id+"F26.imprint","IMPRINT",EDGE,{"derivedFrom":sQuery(id+"F26.wireOp",EDGE,"E45.3.0.0")}),-1.0]])]});
            var Q4;
            Q4=makeQuery(id+"F26.imprint","IMPRINT",FACE,{"disambiguationData":[TD([[makeQuery(id+"F26.imprint","IMPRINT",EDGE,{"derivedFrom":sQuery(id+"F26.wireOp",EDGE,"E45.4.0.0")}),-1.0]])]});
            var Q5;
            Q5=makeQuery(id+"F26.imprint","IMPRINT",FACE,{"disambiguationData":[TD([[makeQuery(id+"F26.imprint","IMPRINT",EDGE,{"derivedFrom":sQuery(id+"F26.wireOp",EDGE,"E45.7.0.0")}),-1.0]])]});
            var Q6;
            Q6=makeQuery(id+"F26.imprint","IMPRINT",FACE,{"disambiguationData":[TD([[makeQuery(id+"F26.imprint","IMPRINT",EDGE,{"derivedFrom":sQuery(id+"F26.wireOp",EDGE,"E45.6.0.0")}),-1.0]])]});
            var Q7;
            Q7=makeQuery(id+"F26.imprint","IMPRINT",FACE,{"disambiguationData":[TD([[makeQuery(id+"F26.imprint","IMPRINT",EDGE,{"derivedFrom":sQuery(id+"F26.wireOp",EDGE,"E45.5.0.0")}),-1.0]])]});
            extrude(context, id + "F27", {"entities" : qUnion([Q0, Q1, Q2, Q3, Q4, Q5, Q6, Q7]), "operationType" : NewBodyOperationType.REMOVE, "oppositeDirection" : true, "depth" : 25.4 * mm, "offsetDistance" : 25.4 * mm});
        }
    });
